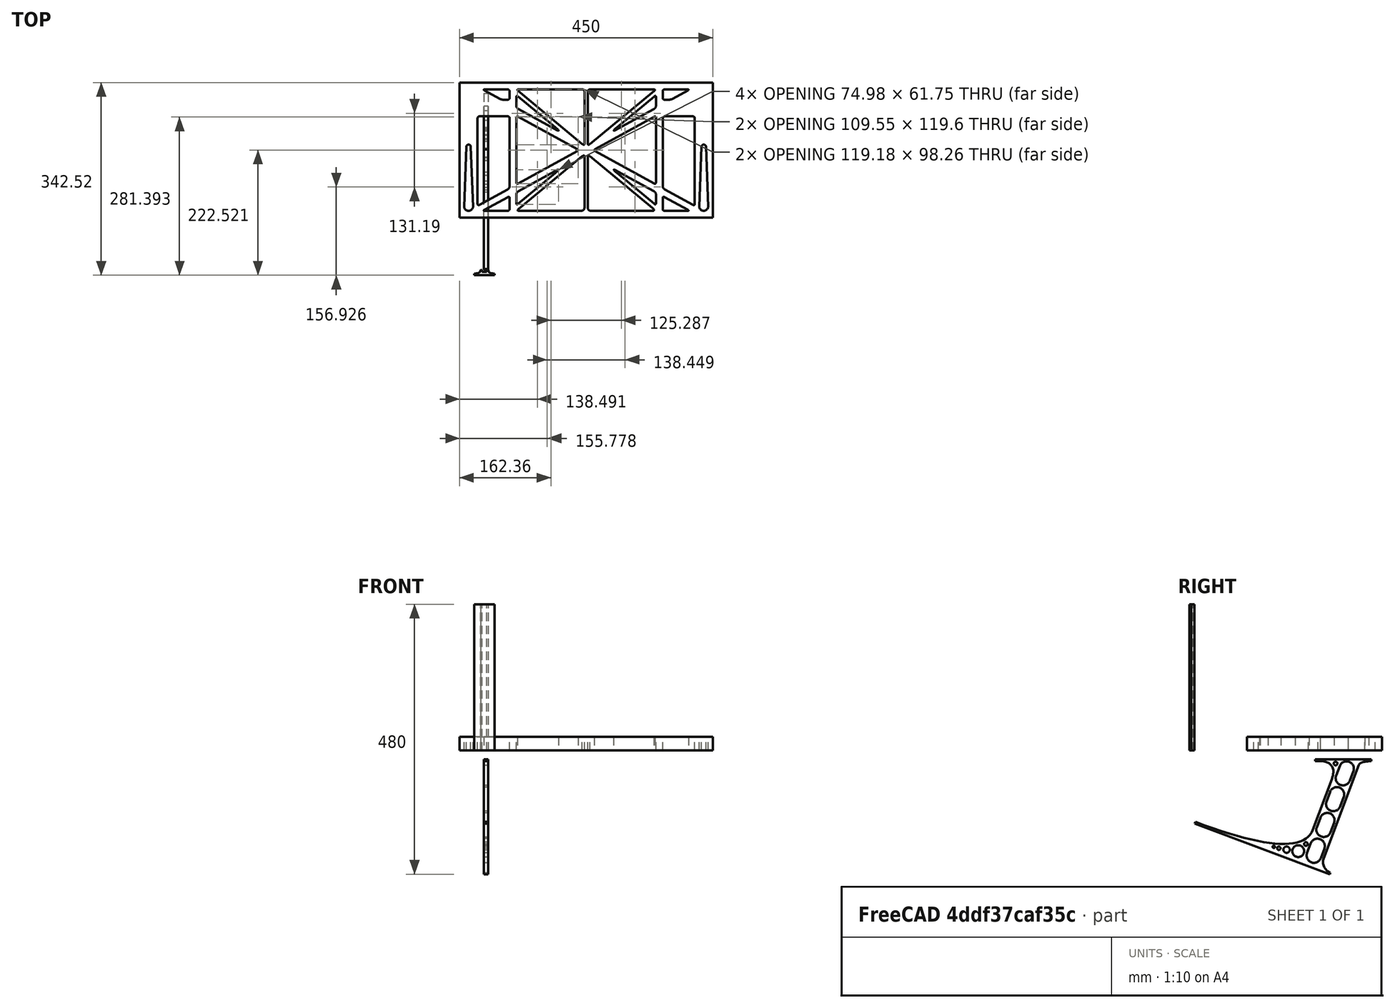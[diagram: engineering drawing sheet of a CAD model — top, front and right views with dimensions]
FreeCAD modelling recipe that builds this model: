
FCSTD DOCUMENT  (FreeCAD 0.19R0.19.2)
Label: laptopStand177FCStd
License: All rights reserved
LicenseURL: http://en.wikipedia.org/wiki/All_rights_reserved
objects: Sketcher::SketchObject×4, Part::Extrusion×3
note: 7 computed .brp shape members not serialized (recipe doc carries the construction recipe); baked Part::Feature solids carry a one-line shape summary decoded from their .brp

FEATURE [Sketcher::SketchObject] Sketch
  FullyConstrained = false
  sketch-geometry (349):
    g0: LineSegment StartX=-10.9272 StartY=-82.7794 StartZ=0 EndX=46.0728 EndY=-51.4823 EndZ=0
    g1: LineSegment StartX=-10.9272 StartY=76.4095 StartZ=0 EndX=-10.9272 EndY=-82.7794 EndZ=0
    g2: LineSegment StartX=46.0728 StartY=76.4095 StartZ=0 EndX=46.0728 EndY=-51.4823 EndZ=0
    g3: LineSegment StartX=-42.9272 StartY=136.221 StartZ=0 EndX=-42.9272 EndY=-103.779 EndZ=0
    g4: LineSegment StartX=407.073 StartY=136.221 StartZ=0 EndX=407.073 EndY=-103.779 EndZ=0
    g5: ArcOfCircle CenterX=-26.9272 CenterY=-83.7794 CenterZ=0 NormalX=0 NormalY=0 NormalZ=1 AngleXU=0 Radius=8 StartAngle=3.14159 EndAngle=6.28319
    g6: ArcOfCircle CenterX=391.073 CenterY=22.1087 CenterZ=0 NormalX=0 NormalY=0 NormalZ=1 AngleXU=0 Radius=8 StartAngle=-4.4e-15 EndAngle=3.14159
    g7: LineSegment StartX=399.073 StartY=22.1087 StartZ=0 EndX=399.073 EndY=-83.7794 EndZ=0
    g8: LineSegment StartX=383.073 StartY=22.1087 StartZ=0 EndX=383.073 EndY=-83.7794 EndZ=0
    g9: ArcOfCircle CenterX=391.073 CenterY=-83.7794 CenterZ=0 NormalX=0 NormalY=0 NormalZ=1 AngleXU=0 Radius=8 StartAngle=3.14159 EndAngle=6.28319
    g10: Circle CenterX=175.022 CenterY=27.0628 CenterZ=0 NormalX=0 NormalY=0 NormalZ=1 AngleXU=0 Radius=1
    g11: Circle CenterX=179.022 CenterY=24.8665 CenterZ=0 NormalX=0 NormalY=0 NormalZ=1 AngleXU=0 Radius=1
    g12: Circle CenterX=179.022 CenterY=27.0628 CenterZ=0 NormalX=0 NormalY=0 NormalZ=1 AngleXU=0 Radius=1
    g13: BSplineCurve PolesCount=3 KnotsCount=2 Degree=2 IsPeriodic=0
    g14: GeomPoint X=175.022 Y=27.0628 Z=0
    g15: GeomPoint X=179.022 Y=27.0628 Z=0
    g16: Circle CenterX=189.124 CenterY=27.0628 CenterZ=0 NormalX=0 NormalY=0 NormalZ=1 AngleXU=0 Radius=1
    g17: Circle CenterX=185.124 CenterY=24.8665 CenterZ=0 NormalX=0 NormalY=0 NormalZ=1 AngleXU=0 Radius=1
    g18: Circle CenterX=185.124 CenterY=27.0628 CenterZ=0 NormalX=0 NormalY=0 NormalZ=1 AngleXU=0 Radius=1
    g19: BSplineCurve PolesCount=3 KnotsCount=2 Degree=2 IsPeriodic=0
    g20: GeomPoint X=189.124 Y=27.0628 Z=0
    g21: GeomPoint X=185.124 Y=27.0628 Z=0
    g22: Circle CenterX=175.022 CenterY=5.37834 CenterZ=0 NormalX=0 NormalY=0 NormalZ=1 AngleXU=0 Radius=1
    g23: Circle CenterX=179.022 CenterY=7.57463 CenterZ=0 NormalX=0 NormalY=0 NormalZ=1 AngleXU=0 Radius=1
    g24: Circle CenterX=179.022 CenterY=5.34704 CenterZ=0 NormalX=0 NormalY=0 NormalZ=1 AngleXU=0 Radius=1
    g25: BSplineCurve PolesCount=3 KnotsCount=2 Degree=2 IsPeriodic=0
    g26: GeomPoint X=175.022 Y=5.37834 Z=0
    g27: GeomPoint X=179.022 Y=5.34704 Z=0
    g28: Circle CenterX=189.124 CenterY=5.37834 CenterZ=0 NormalX=0 NormalY=0 NormalZ=1 AngleXU=0 Radius=1
    g29: Circle CenterX=185.124 CenterY=7.57463 CenterZ=0 NormalX=0 NormalY=0 NormalZ=1 AngleXU=0 Radius=1
    g30: Circle CenterX=185.124 CenterY=5.34704 CenterZ=0 NormalX=0 NormalY=0 NormalZ=1 AngleXU=0 Radius=1
    g31: BSplineCurve PolesCount=3 KnotsCount=2 Degree=2 IsPeriodic=0
    g32: GeomPoint X=189.124 Y=5.37834 Z=0
    g33: GeomPoint X=185.124 Y=5.34704 Z=0
    g34: Circle CenterX=165.871 CenterY=18.1458 CenterZ=0 NormalX=0 NormalY=0 NormalZ=1 AngleXU=0 Radius=1
    g35: Circle CenterX=169.377 CenterY=16.2206 CenterZ=0 NormalX=0 NormalY=0 NormalZ=1 AngleXU=0 Radius=1
    g36: Circle CenterX=165.871 CenterY=14.2954 CenterZ=0 NormalX=0 NormalY=0 NormalZ=1 AngleXU=0 Radius=1
    g37: BSplineCurve PolesCount=3 KnotsCount=2 Degree=2 IsPeriodic=0
    g38: GeomPoint X=165.871 Y=18.1458 Z=0
    g39: GeomPoint X=165.871 Y=14.2954 Z=0
    g40: Circle CenterX=198.275 CenterY=18.1458 CenterZ=0 NormalX=0 NormalY=0 NormalZ=1 AngleXU=0 Radius=1
    g41: Circle CenterX=194.768 CenterY=16.2206 CenterZ=0 NormalX=0 NormalY=0 NormalZ=1 AngleXU=0 Radius=1
    g42: Circle CenterX=198.275 CenterY=14.2954 CenterZ=0 NormalX=0 NormalY=0 NormalZ=1 AngleXU=0 Radius=1
    g43: BSplineCurve PolesCount=3 KnotsCount=2 Degree=2 IsPeriodic=0
    g44: GeomPoint X=198.275 Y=18.1458 Z=0
    g45: GeomPoint X=198.275 Y=14.2954 Z=0
    g46: LineSegment StartX=407.073 StartY=-103.779 StartZ=0 EndX=-42.9272 EndY=-103.779 EndZ=0
    g47: LineSegment StartX=407.073 StartY=136.221 StartZ=0 EndX=-42.9272 EndY=136.221 EndZ=0
    g48: LineSegment StartX=46.0728 StartY=76.4095 StartZ=0 EndX=-10.9272 EndY=76.4095 EndZ=0
    g49: Circle CenterX=125.607 CenterY=54.1951 CenterZ=0 NormalX=0 NormalY=0 NormalZ=1 AngleXU=0 Radius=1
    g50: Circle CenterX=139.632 CenterY=46.4944 CenterZ=0 NormalX=0 NormalY=0 NormalZ=1 AngleXU=0 Radius=1
    g51: Circle CenterX=127.326 CenterY=56.7187 CenterZ=0 NormalX=0 NormalY=0 NormalZ=1 AngleXU=0 Radius=1
    g52: BSplineCurve PolesCount=3 KnotsCount=2 Degree=2 IsPeriodic=0
    g53: GeomPoint X=125.607 Y=54.1951 Z=0
    g54: GeomPoint X=127.326 Y=56.7187 Z=0
    g55: Circle CenterX=236.821 CenterY=56.7187 CenterZ=0 NormalX=0 NormalY=0 NormalZ=1 AngleXU=0 Radius=1
    g56: Circle CenterX=224.513 CenterY=46.4944 CenterZ=0 NormalX=0 NormalY=0 NormalZ=1 AngleXU=0 Radius=1
    g57: Circle CenterX=238.538 CenterY=54.1951 CenterZ=0 NormalX=0 NormalY=0 NormalZ=1 AngleXU=0 Radius=1
    g58: BSplineCurve PolesCount=3 KnotsCount=2 Degree=2 IsPeriodic=0
    g59: GeomPoint X=236.821 Y=56.7187 Z=0
    g60: GeomPoint X=238.538 Y=54.1951 Z=0
    g61: Circle CenterX=238.538 CenterY=-21.7539 CenterZ=0 NormalX=0 NormalY=0 NormalZ=1 AngleXU=0 Radius=1
    g62: Circle CenterX=224.513 CenterY=-14.0532 CenterZ=0 NormalX=0 NormalY=0 NormalZ=1 AngleXU=0 Radius=1
    g63: Circle CenterX=236.821 CenterY=-24.2775 CenterZ=0 NormalX=0 NormalY=0 NormalZ=1 AngleXU=0 Radius=1
    g64: BSplineCurve PolesCount=3 KnotsCount=2 Degree=2 IsPeriodic=0
    g65: GeomPoint X=238.538 Y=-21.7539 Z=0
    g66: GeomPoint X=236.821 Y=-24.2775 Z=0
    g67: Circle CenterX=125.607 CenterY=-21.7539 CenterZ=0 NormalX=0 NormalY=0 NormalZ=1 AngleXU=0 Radius=1
    g68: Circle CenterX=139.632 CenterY=-14.0532 CenterZ=0 NormalX=0 NormalY=0 NormalZ=1 AngleXU=0 Radius=1
    g69: Circle CenterX=127.325 CenterY=-24.2775 CenterZ=0 NormalX=0 NormalY=0 NormalZ=1 AngleXU=0 Radius=1
    g70: BSplineCurve PolesCount=3 KnotsCount=2 Degree=2 IsPeriodic=0
    g71: GeomPoint X=125.607 Y=-21.7539 Z=0
    g72: GeomPoint X=127.325 Y=-24.2775 Z=0
    g73: Circle CenterX=302.996 CenterY=111.695 CenterZ=0 NormalX=0 NormalY=0 NormalZ=1 AngleXU=0 Radius=1
    g74: Circle CenterX=306.073 CenterY=114.251 CenterZ=0 NormalX=0 NormalY=0 NormalZ=1 AngleXU=0 Radius=1
    g75: Circle CenterX=306.073 CenterY=110.251 CenterZ=0 NormalX=0 NormalY=0 NormalZ=1 AngleXU=0 Radius=1
    g76: BSplineCurve PolesCount=3 KnotsCount=2 Degree=2 IsPeriodic=0
    g77: GeomPoint X=302.996 Y=111.695 Z=0
    g78: GeomPoint X=306.073 Y=110.251 Z=0
    g79: Circle CenterX=306.073 CenterY=95.2763 CenterZ=0 NormalX=0 NormalY=0 NormalZ=1 AngleXU=0 Radius=1
    g80: Circle CenterX=306.073 CenterY=91.2763 CenterZ=0 NormalX=0 NormalY=0 NormalZ=1 AngleXU=0 Radius=1
    g81: Circle CenterX=302.567 CenterY=89.3511 CenterZ=0 NormalX=0 NormalY=0 NormalZ=1 AngleXU=0 Radius=1
    g82: BSplineCurve PolesCount=3 KnotsCount=2 Degree=2 IsPeriodic=0
    g83: GeomPoint X=306.073 Y=95.2763 Z=0
    g84: GeomPoint X=302.567 Y=89.3511 Z=0
    g85: LineSegment StartX=306.073 StartY=110.251 StartZ=0 EndX=306.073 EndY=95.2763 EndZ=0
    g86: LineSegment StartX=302.996 StartY=111.695 StartZ=0 EndX=236.821 EndY=56.7187 EndZ=0
    g87: LineSegment StartX=238.538 StartY=54.1951 StartZ=0 EndX=302.567 EndY=89.3511 EndZ=0
    g88: Circle CenterX=61.1496 CenterY=111.695 CenterZ=0 NormalX=0 NormalY=0 NormalZ=1 AngleXU=0 Radius=1
    g89: Circle CenterX=58.0728 CenterY=114.251 CenterZ=0 NormalX=0 NormalY=0 NormalZ=1 AngleXU=0 Radius=1
    g90: Circle CenterX=58.0728 CenterY=110.251 CenterZ=0 NormalX=0 NormalY=0 NormalZ=1 AngleXU=0 Radius=1
    g91: BSplineCurve PolesCount=3 KnotsCount=2 Degree=2 IsPeriodic=0
    g92: GeomPoint X=61.1496 Y=111.695 Z=0
    g93: GeomPoint X=58.0728 Y=110.251 Z=0
    g94: Circle CenterX=61.5791 CenterY=89.3511 CenterZ=0 NormalX=0 NormalY=0 NormalZ=1 AngleXU=0 Radius=1
    g95: Circle CenterX=58.0728 CenterY=91.2763 CenterZ=0 NormalX=0 NormalY=0 NormalZ=1 AngleXU=0 Radius=1
    g96: Circle CenterX=58.0728 CenterY=95.2763 CenterZ=0 NormalX=0 NormalY=0 NormalZ=1 AngleXU=0 Radius=1
    g97: BSplineCurve PolesCount=3 KnotsCount=2 Degree=2 IsPeriodic=0
    g98: GeomPoint X=61.5791 Y=89.3511 Z=0
    g99: GeomPoint X=58.0728 Y=95.2763 Z=0
    g100: LineSegment StartX=58.0728 StartY=110.251 StartZ=0 EndX=58.0728 EndY=95.2763 EndZ=0
    g101: LineSegment StartX=61.1496 StartY=111.695 StartZ=0 EndX=127.326 EndY=56.7187 EndZ=0
    g102: LineSegment StartX=125.607 StartY=54.1951 StartZ=0 EndX=61.5791 EndY=89.3511 EndZ=0
    g103: Circle CenterX=61.5791 CenterY=-56.9099 CenterZ=0 NormalX=0 NormalY=0 NormalZ=1 AngleXU=0 Radius=1
    g104: Circle CenterX=58.0728 CenterY=-58.8351 CenterZ=0 NormalX=0 NormalY=0 NormalZ=1 AngleXU=0 Radius=1
    g105: Circle CenterX=58.0728 CenterY=-62.8351 CenterZ=0 NormalX=0 NormalY=0 NormalZ=1 AngleXU=0 Radius=1
    g106: BSplineCurve PolesCount=3 KnotsCount=2 Degree=2 IsPeriodic=0
    g107: GeomPoint X=61.5791 Y=-56.9099 Z=0
    g108: GeomPoint X=58.0728 Y=-62.8351 Z=0
    g109: Circle CenterX=58.0728 CenterY=-77.8102 CenterZ=0 NormalX=0 NormalY=0 NormalZ=1 AngleXU=0 Radius=1
    g110: Circle CenterX=58.0728 CenterY=-81.8102 CenterZ=0 NormalX=0 NormalY=0 NormalZ=1 AngleXU=0 Radius=1
    g111: Circle CenterX=61.1496 CenterY=-79.2541 CenterZ=0 NormalX=0 NormalY=0 NormalZ=1 AngleXU=0 Radius=1
    g112: BSplineCurve PolesCount=3 KnotsCount=2 Degree=2 IsPeriodic=0
    g113: GeomPoint X=58.0728 Y=-77.8102 Z=0
    g114: GeomPoint X=61.1496 Y=-79.2541 Z=0
    g115: LineSegment StartX=58.0728 StartY=-62.8351 StartZ=0 EndX=58.0728 EndY=-77.8102 EndZ=0
    g116: LineSegment StartX=61.1496 StartY=-79.2541 StartZ=0 EndX=127.325 EndY=-24.2775 EndZ=0
    g117: LineSegment StartX=125.607 StartY=-21.7539 StartZ=0 EndX=61.5791 EndY=-56.9099 EndZ=0
    g118: Circle CenterX=302.567 CenterY=-56.9099 CenterZ=0 NormalX=0 NormalY=0 NormalZ=1 AngleXU=0 Radius=1
    g119: Circle CenterX=306.073 CenterY=-58.8351 CenterZ=0 NormalX=0 NormalY=0 NormalZ=1 AngleXU=0 Radius=1
    g120: Circle CenterX=306.073 CenterY=-62.8351 CenterZ=0 NormalX=0 NormalY=0 NormalZ=1 AngleXU=0 Radius=1
    g121: BSplineCurve PolesCount=3 KnotsCount=2 Degree=2 IsPeriodic=0
    g122: GeomPoint X=302.567 Y=-56.9099 Z=0
    g123: GeomPoint X=306.073 Y=-62.8351 Z=0
    g124: Circle CenterX=302.996 CenterY=-79.2541 CenterZ=0 NormalX=0 NormalY=0 NormalZ=1 AngleXU=0 Radius=1
    g125: Circle CenterX=306.073 CenterY=-81.8102 CenterZ=0 NormalX=0 NormalY=0 NormalZ=1 AngleXU=0 Radius=1
    g126: Circle CenterX=306.073 CenterY=-77.8102 CenterZ=0 NormalX=0 NormalY=0 NormalZ=1 AngleXU=0 Radius=1
    g127: BSplineCurve PolesCount=3 KnotsCount=2 Degree=2 IsPeriodic=0
    g128: GeomPoint X=302.996 Y=-79.2541 Z=0
    g129: GeomPoint X=306.073 Y=-77.8102 Z=0
    g130: LineSegment StartX=306.073 StartY=-62.8351 StartZ=0 EndX=306.073 EndY=-77.8102 EndZ=0
    g131: LineSegment StartX=302.996 StartY=-79.2541 StartZ=0 EndX=236.821 EndY=-24.2775 EndZ=0
    g132: LineSegment StartX=238.538 StartY=-21.7539 StartZ=0 EndX=302.567 EndY=-56.9099 EndZ=0
    g133: Circle CenterX=61.6457 CenterY=-88.8112 CenterZ=0 NormalX=0 NormalY=0 NormalZ=1 AngleXU=0 Radius=1
    g134: Circle CenterX=58.0728 CenterY=-91.7794 CenterZ=0 NormalX=0 NormalY=0 NormalZ=1 AngleXU=0 Radius=1
    g135: Circle CenterX=63.9135 CenterY=-91.7794 CenterZ=0 NormalX=0 NormalY=0 NormalZ=1 AngleXU=0 Radius=1
    g136: BSplineCurve PolesCount=3 KnotsCount=2 Degree=2 IsPeriodic=0
    g137: GeomPoint X=61.6457 Y=-88.8112 Z=0
    g138: GeomPoint X=63.9135 Y=-91.7794 Z=0
    g139: Circle CenterX=179.022 CenterY=-85.8163 CenterZ=0 NormalX=0 NormalY=0 NormalZ=1 AngleXU=0 Radius=1
    g140: Circle CenterX=179.022 CenterY=-91.7794 CenterZ=0 NormalX=0 NormalY=0 NormalZ=1 AngleXU=0 Radius=1
    g141: Circle CenterX=171.895 CenterY=-91.7794 CenterZ=0 NormalX=0 NormalY=0 NormalZ=1 AngleXU=0 Radius=1
    g142: BSplineCurve PolesCount=3 KnotsCount=2 Degree=2 IsPeriodic=0
    g143: GeomPoint X=179.022 Y=-85.8163 Z=0
    g144: GeomPoint X=171.895 Y=-91.7794 Z=0
    g145: Circle CenterX=185.124 CenterY=-86.2028 CenterZ=0 NormalX=0 NormalY=0 NormalZ=1 AngleXU=0 Radius=1
    g146: Circle CenterX=185.124 CenterY=-91.7794 CenterZ=0 NormalX=0 NormalY=0 NormalZ=1 AngleXU=0 Radius=1
    g147: Circle CenterX=191.747 CenterY=-91.7794 CenterZ=0 NormalX=0 NormalY=0 NormalZ=1 AngleXU=0 Radius=1
    g148: BSplineCurve PolesCount=3 KnotsCount=2 Degree=2 IsPeriodic=0
    g149: GeomPoint X=185.124 Y=-86.2028 Z=0
    g150: GeomPoint X=191.747 Y=-91.7794 Z=0
    g151: Circle CenterX=299.888 CenterY=-86.6413 CenterZ=0 NormalX=0 NormalY=0 NormalZ=1 AngleXU=0 Radius=1
    g152: Circle CenterX=306.073 CenterY=-91.7794 CenterZ=0 NormalX=0 NormalY=0 NormalZ=1 AngleXU=0 Radius=1
    g153: Circle CenterX=298.776 CenterY=-91.7794 CenterZ=0 NormalX=0 NormalY=0 NormalZ=1 AngleXU=0 Radius=1
    g154: BSplineCurve PolesCount=3 KnotsCount=2 Degree=2 IsPeriodic=0
    g155: GeomPoint X=299.888 Y=-86.6413 Z=0
    g156: GeomPoint X=298.776 Y=-91.7794 Z=0
    g157: LineSegment StartX=189.124 StartY=5.37834 StartZ=0 EndX=299.888 EndY=-86.6413 EndZ=0
    g158: LineSegment StartX=298.776 StartY=-91.7794 StartZ=0 EndX=191.747 EndY=-91.7794 EndZ=0
    g159: LineSegment StartX=185.124 StartY=-86.2028 StartZ=0 EndX=185.124 EndY=5.34704 EndZ=0
    g160: LineSegment StartX=179.022 StartY=5.34704 StartZ=0 EndX=179.022 EndY=-85.8163 EndZ=0
    g161: LineSegment StartX=171.895 StartY=-91.7794 StartZ=0 EndX=63.9135 EndY=-91.7794 EndZ=0
    g162: LineSegment StartX=61.6457 StartY=-88.8112 StartZ=0 EndX=175.022 EndY=5.37834 EndZ=0
    g163: Circle CenterX=302.073 CenterY=124.221 CenterZ=0 NormalX=0 NormalY=0 NormalZ=1 AngleXU=0 Radius=1
    g164: Circle CenterX=306.073 CenterY=124.221 CenterZ=0 NormalX=0 NormalY=0 NormalZ=1 AngleXU=0 Radius=1
    g165: Circle CenterX=302.996 CenterY=121.665 CenterZ=0 NormalX=0 NormalY=0 NormalZ=1 AngleXU=0 Radius=1
    g166: BSplineCurve PolesCount=3 KnotsCount=2 Degree=2 IsPeriodic=0
    g167: GeomPoint X=302.073 Y=124.221 Z=0
    g168: GeomPoint X=302.996 Y=121.665 Z=0
    g169: Circle CenterX=189.124 CenterY=124.221 CenterZ=0 NormalX=0 NormalY=0 NormalZ=1 AngleXU=0 Radius=1
    g170: Circle CenterX=185.124 CenterY=124.221 CenterZ=0 NormalX=0 NormalY=0 NormalZ=1 AngleXU=0 Radius=1
    g171: Circle CenterX=185.124 CenterY=120.221 CenterZ=0 NormalX=0 NormalY=0 NormalZ=1 AngleXU=0 Radius=1
    g172: BSplineCurve PolesCount=3 KnotsCount=2 Degree=2 IsPeriodic=0
    g173: GeomPoint X=189.124 Y=124.221 Z=0
    g174: GeomPoint X=185.124 Y=120.221 Z=0
    g175: Circle CenterX=175.022 CenterY=124.221 CenterZ=0 NormalX=0 NormalY=0 NormalZ=1 AngleXU=0 Radius=1
    g176: Circle CenterX=179.022 CenterY=124.221 CenterZ=0 NormalX=0 NormalY=0 NormalZ=1 AngleXU=0 Radius=1
    g177: Circle CenterX=179.022 CenterY=120.221 CenterZ=0 NormalX=0 NormalY=0 NormalZ=1 AngleXU=0 Radius=1
    g178: BSplineCurve PolesCount=3 KnotsCount=2 Degree=2 IsPeriodic=0
    g179: GeomPoint X=175.022 Y=124.221 Z=0
    g180: GeomPoint X=179.022 Y=120.221 Z=0
    g181: Circle CenterX=62.0728 CenterY=124.221 CenterZ=0 NormalX=0 NormalY=0 NormalZ=1 AngleXU=0 Radius=1
    g182: Circle CenterX=58.0728 CenterY=124.221 CenterZ=0 NormalX=0 NormalY=0 NormalZ=1 AngleXU=0 Radius=1
    g183: Circle CenterX=61.1496 CenterY=121.665 CenterZ=0 NormalX=0 NormalY=0 NormalZ=1 AngleXU=0 Radius=1
    g184: BSplineCurve PolesCount=3 KnotsCount=2 Degree=2 IsPeriodic=0
    g185: GeomPoint X=62.0728 Y=124.221 Z=0
    g186: GeomPoint X=61.1496 Y=121.665 Z=0
    g187: LineSegment StartX=62.0728 StartY=124.221 StartZ=0 EndX=175.022 EndY=124.221 EndZ=0
    g188: LineSegment StartX=179.022 StartY=120.221 StartZ=0 EndX=179.022 EndY=27.0628 EndZ=0
    g189: LineSegment StartX=185.124 StartY=27.0628 StartZ=0 EndX=185.124 EndY=120.221 EndZ=0
    g190: LineSegment StartX=189.124 StartY=124.221 StartZ=0 EndX=302.073 EndY=124.221 EndZ=0
    g191: LineSegment StartX=302.996 StartY=121.665 StartZ=0 EndX=189.124 EndY=27.0628 EndZ=0
    g192: LineSegment StartX=175.022 StartY=27.0628 StartZ=0 EndX=61.1496 EndY=121.665 EndZ=0
    g193: Circle CenterX=61.5791 CenterY=75.4095 CenterZ=0 NormalX=0 NormalY=0 NormalZ=1 AngleXU=0 Radius=1
    g194: Circle CenterX=58.0728 CenterY=77.3346 CenterZ=0 NormalX=0 NormalY=0 NormalZ=1 AngleXU=0 Radius=1
    g195: Circle CenterX=58.0728 CenterY=73.3346 CenterZ=0 NormalX=0 NormalY=0 NormalZ=1 AngleXU=0 Radius=1
    g196: BSplineCurve PolesCount=3 KnotsCount=2 Degree=2 IsPeriodic=0
    g197: GeomPoint X=61.5791 Y=75.4095 Z=0
    g198: GeomPoint X=58.0728 Y=73.3346 Z=0
    g199: Circle CenterX=58.0728 CenterY=-40.8935 CenterZ=0 NormalX=0 NormalY=0 NormalZ=1 AngleXU=0 Radius=1
    g200: Circle CenterX=58.0728 CenterY=-44.8935 CenterZ=0 NormalX=0 NormalY=0 NormalZ=1 AngleXU=0 Radius=1
    g201: Circle CenterX=61.5791 CenterY=-42.9683 CenterZ=0 NormalX=0 NormalY=0 NormalZ=1 AngleXU=0 Radius=1
    g202: BSplineCurve PolesCount=3 KnotsCount=2 Degree=2 IsPeriodic=0
    g203: GeomPoint X=58.0728 Y=-40.8935 Z=0
    g204: GeomPoint X=61.5791 Y=-42.9683 Z=0
    g205: LineSegment StartX=61.5791 StartY=-42.9683 StartZ=0 EndX=165.871 EndY=14.2954 EndZ=0
    g206: LineSegment StartX=165.871 StartY=18.1458 StartZ=0 EndX=61.5791 EndY=75.4095 EndZ=0
    g207: LineSegment StartX=58.0728 StartY=73.3346 StartZ=0 EndX=58.0728 EndY=-40.8935 EndZ=0
    g208: Circle CenterX=302.567 CenterY=-42.9683 CenterZ=0 NormalX=0 NormalY=0 NormalZ=1 AngleXU=0 Radius=1
    g209: Circle CenterX=306.073 CenterY=-44.8935 CenterZ=0 NormalX=0 NormalY=0 NormalZ=1 AngleXU=0 Radius=1
    g210: Circle CenterX=306.073 CenterY=-40.8935 CenterZ=0 NormalX=0 NormalY=0 NormalZ=1 AngleXU=0 Radius=1
    g211: BSplineCurve PolesCount=3 KnotsCount=2 Degree=2 IsPeriodic=0
    g212: GeomPoint X=302.567 Y=-42.9683 Z=0
    g213: GeomPoint X=306.073 Y=-40.8935 Z=0
    g214: Circle CenterX=306.073 CenterY=73.3346 CenterZ=0 NormalX=0 NormalY=0 NormalZ=1 AngleXU=0 Radius=1
    g215: Circle CenterX=306.073 CenterY=77.3346 CenterZ=0 NormalX=0 NormalY=0 NormalZ=1 AngleXU=0 Radius=1
    g216: Circle CenterX=302.567 CenterY=75.4095 CenterZ=0 NormalX=0 NormalY=0 NormalZ=1 AngleXU=0 Radius=1
    g217: BSplineCurve PolesCount=3 KnotsCount=2 Degree=2 IsPeriodic=0
    g218: GeomPoint X=306.073 Y=73.3346 Z=0
    g219: GeomPoint X=302.567 Y=75.4095 Z=0
    g220: LineSegment StartX=302.567 StartY=-42.9683 StartZ=0 EndX=198.275 EndY=14.2954 EndZ=0
    g221: LineSegment StartX=198.275 StartY=18.1458 StartZ=0 EndX=302.567 EndY=75.4095 EndZ=0
    g222: LineSegment StartX=306.073 StartY=73.3346 StartZ=0 EndX=306.073 EndY=-40.8935 EndZ=0
    g223: LineSegment StartX=322.073 StartY=105.865 StartZ=0 EndX=328.643 EndY=105.865 EndZ=0
    g224: LineSegment StartX=318.073 StartY=120.221 StartZ=0 EndX=318.073 EndY=109.865 EndZ=0
    g225: LineSegment StartX=336.157 StartY=107.779 StartZ=0 EndX=362.567 EndY=122.294 EndZ=0
    g226: Circle CenterX=362.073 CenterY=124.221 CenterZ=0 NormalX=0 NormalY=0 NormalZ=1 AngleXU=0 Radius=1
    g227: Circle CenterX=366.073 CenterY=124.221 CenterZ=0 NormalX=0 NormalY=0 NormalZ=1 AngleXU=0 Radius=1
    g228: Circle CenterX=362.567 CenterY=122.294 CenterZ=0 NormalX=0 NormalY=0 NormalZ=1 AngleXU=0 Radius=1
    g229: BSplineCurve PolesCount=3 KnotsCount=2 Degree=2 IsPeriodic=0
    g230: GeomPoint X=362.073 Y=124.221 Z=0
    g231: GeomPoint X=362.567 Y=122.294 Z=0
    g232: Circle CenterX=322.073 CenterY=124.221 CenterZ=0 NormalX=0 NormalY=0 NormalZ=1 AngleXU=0 Radius=1
    g233: Circle CenterX=318.073 CenterY=124.221 CenterZ=0 NormalX=0 NormalY=0 NormalZ=1 AngleXU=0 Radius=1
    g234: Circle CenterX=318.073 CenterY=120.221 CenterZ=0 NormalX=0 NormalY=0 NormalZ=1 AngleXU=0 Radius=1
    g235: BSplineCurve PolesCount=3 KnotsCount=2 Degree=2 IsPeriodic=0
    g236: GeomPoint X=322.073 Y=124.221 Z=0
    g237: GeomPoint X=318.073 Y=120.221 Z=0
    g238: Circle CenterX=322.073 CenterY=105.865 CenterZ=0 NormalX=0 NormalY=0 NormalZ=1 AngleXU=0 Radius=1
    g239: Circle CenterX=318.073 CenterY=105.865 CenterZ=0 NormalX=0 NormalY=0 NormalZ=1 AngleXU=0 Radius=1
    g240: Circle CenterX=318.073 CenterY=109.865 CenterZ=0 NormalX=0 NormalY=0 NormalZ=1 AngleXU=0 Radius=1
    g241: BSplineCurve PolesCount=3 KnotsCount=2 Degree=2 IsPeriodic=0
    g242: GeomPoint X=322.073 Y=105.865 Z=0
    g243: GeomPoint X=318.073 Y=109.865 Z=0
    g244: Circle CenterX=336.157 CenterY=107.779 CenterZ=0 NormalX=0 NormalY=0 NormalZ=1 AngleXU=0 Radius=1
    g245: Circle CenterX=332.651 CenterY=105.853 CenterZ=0 NormalX=0 NormalY=0 NormalZ=1 AngleXU=0 Radius=1
    g246: Circle CenterX=328.643 CenterY=105.865 CenterZ=0 NormalX=0 NormalY=0 NormalZ=1 AngleXU=0 Radius=1
    g247: BSplineCurve PolesCount=3 KnotsCount=2 Degree=2 IsPeriodic=0
    g248: GeomPoint X=336.157 Y=107.779 Z=0
    g249: GeomPoint X=328.643 Y=105.865 Z=0
    g250: LineSegment StartX=322.073 StartY=124.221 StartZ=0 EndX=362.073 EndY=124.221 EndZ=0
    g251: Circle CenterX=371.567 CenterY=-80.8644 CenterZ=0 NormalX=0 NormalY=0 NormalZ=1 AngleXU=0 Radius=1
    g252: Circle CenterX=375.073 CenterY=-82.7896 CenterZ=0 NormalX=0 NormalY=0 NormalZ=1 AngleXU=0 Radius=1
    g253: Circle CenterX=375.073 CenterY=-78.7896 CenterZ=0 NormalX=0 NormalY=0 NormalZ=1 AngleXU=0 Radius=1
    g254: BSplineCurve PolesCount=3 KnotsCount=2 Degree=2 IsPeriodic=0
    g255: GeomPoint X=371.567 Y=-80.8644 Z=0
    g256: GeomPoint X=375.073 Y=-78.7896 Z=0
    g257: Circle CenterX=321.579 CenterY=-53.4075 CenterZ=0 NormalX=0 NormalY=0 NormalZ=1 AngleXU=0 Radius=1
    g258: Circle CenterX=318.073 CenterY=-51.4823 CenterZ=0 NormalX=0 NormalY=0 NormalZ=1 AngleXU=0 Radius=1
    g259: Circle CenterX=318.073 CenterY=-47.4805 CenterZ=0 NormalX=0 NormalY=0 NormalZ=1 AngleXU=0 Radius=1
    g260: BSplineCurve PolesCount=3 KnotsCount=2 Degree=2 IsPeriodic=0
    g261: GeomPoint X=321.579 Y=-53.4075 Z=0
    g262: GeomPoint X=318.073 Y=-47.4805 Z=0
    g263: LineSegment StartX=371.567 StartY=-80.8644 StartZ=0 EndX=321.579 EndY=-53.4075 EndZ=0
    g264: Circle CenterX=321.579 CenterY=-67.3492 CenterZ=0 NormalX=0 NormalY=0 NormalZ=1 AngleXU=0 Radius=1
    g265: Circle CenterX=318.073 CenterY=-65.424 CenterZ=0 NormalX=0 NormalY=0 NormalZ=1 AngleXU=0 Radius=1
    g266: Circle CenterX=318.073 CenterY=-69.424 CenterZ=0 NormalX=0 NormalY=0 NormalZ=1 AngleXU=0 Radius=1
    g267: BSplineCurve PolesCount=3 KnotsCount=2 Degree=2 IsPeriodic=0
    g268: GeomPoint X=321.579 Y=-67.3492 Z=0
    g269: GeomPoint X=318.073 Y=-69.424 Z=0
    g270: Circle CenterX=362.567 CenterY=-89.8542 CenterZ=0 NormalX=0 NormalY=0 NormalZ=1 AngleXU=0 Radius=1
    g271: Circle CenterX=366.073 CenterY=-91.7794 CenterZ=0 NormalX=0 NormalY=0 NormalZ=1 AngleXU=0 Radius=1
    g272: Circle CenterX=362.073 CenterY=-91.7794 CenterZ=0 NormalX=0 NormalY=0 NormalZ=1 AngleXU=0 Radius=1
    g273: BSplineCurve PolesCount=3 KnotsCount=2 Degree=2 IsPeriodic=0
    g274: GeomPoint X=362.567 Y=-89.8542 Z=0
    g275: GeomPoint X=362.073 Y=-91.7794 Z=0
    g276: Circle CenterX=322.073 CenterY=-91.7794 CenterZ=0 NormalX=0 NormalY=0 NormalZ=1 AngleXU=0 Radius=1
    g277: Circle CenterX=318.073 CenterY=-91.7794 CenterZ=0 NormalX=0 NormalY=0 NormalZ=1 AngleXU=0 Radius=1
    g278: Circle CenterX=318.073 CenterY=-87.7794 CenterZ=0 NormalX=0 NormalY=0 NormalZ=1 AngleXU=0 Radius=1
    g279: BSplineCurve PolesCount=3 KnotsCount=2 Degree=2 IsPeriodic=0
    g280: GeomPoint X=322.073 Y=-91.7794 Z=0
    g281: GeomPoint X=318.073 Y=-87.7794 Z=0
    g282: LineSegment StartX=362.567 StartY=-89.8542 StartZ=0 EndX=321.579 EndY=-67.3492 EndZ=0
    g283: LineSegment StartX=318.073 StartY=-69.424 StartZ=0 EndX=318.073 EndY=-87.7794 EndZ=0
    g284: LineSegment StartX=322.073 StartY=-91.7794 StartZ=0 EndX=362.073 EndY=-91.7794 EndZ=0
    g285: Circle CenterX=2.07281 CenterY=124.221 CenterZ=0 NormalX=0 NormalY=0 NormalZ=1 AngleXU=0 Radius=1
    g286: Circle CenterX=1.57905 CenterY=122.295 CenterZ=0 NormalX=0 NormalY=0 NormalZ=1 AngleXU=0 Radius=1
    g287: BSplineCurve PolesCount=3 KnotsCount=2 Degree=2 IsPeriodic=0
    g288: GeomPoint X=2.07281 Y=124.221 Z=0
    g289: GeomPoint X=1.57905 Y=122.295 Z=0
    g290: Circle CenterX=42.0728 CenterY=124.221 CenterZ=0 NormalX=0 NormalY=0 NormalZ=1 AngleXU=0 Radius=1
    g291: Circle CenterX=46.0728 CenterY=124.221 CenterZ=0 NormalX=0 NormalY=0 NormalZ=1 AngleXU=0 Radius=1
    g292: Circle CenterX=46.0728 CenterY=120.221 CenterZ=0 NormalX=0 NormalY=0 NormalZ=1 AngleXU=0 Radius=1
    g293: BSplineCurve PolesCount=3 KnotsCount=2 Degree=2 IsPeriodic=0
    g294: GeomPoint X=42.0728 Y=124.221 Z=0
    g295: GeomPoint X=46.0728 Y=120.221 Z=0
    g296: Circle CenterX=46.0728 CenterY=109.865 CenterZ=0 NormalX=0 NormalY=0 NormalZ=1 AngleXU=0 Radius=1
    g297: Circle CenterX=46.0728 CenterY=105.865 CenterZ=0 NormalX=0 NormalY=0 NormalZ=1 AngleXU=0 Radius=1
    g298: Circle CenterX=42.0728 CenterY=105.865 CenterZ=0 NormalX=0 NormalY=0 NormalZ=1 AngleXU=0 Radius=1
    g299: BSplineCurve PolesCount=3 KnotsCount=2 Degree=2 IsPeriodic=0
    g300: GeomPoint X=46.0728 Y=109.865 Z=0
    g301: GeomPoint X=42.0728 Y=105.865 Z=0
    g302: Circle CenterX=35.5028 CenterY=105.865 CenterZ=0 NormalX=0 NormalY=0 NormalZ=1 AngleXU=0 Radius=1
    g303: Circle CenterX=31.5028 CenterY=105.865 CenterZ=0 NormalX=0 NormalY=0 NormalZ=1 AngleXU=0 Radius=1
    g304: Circle CenterX=27.9965 CenterY=107.79 CenterZ=0 NormalX=0 NormalY=0 NormalZ=1 AngleXU=0 Radius=1
    g305: BSplineCurve PolesCount=3 KnotsCount=2 Degree=2 IsPeriodic=0
    g306: GeomPoint X=35.5028 Y=105.865 Z=0
    g307: GeomPoint X=27.9965 Y=107.79 Z=0
    g308: LineSegment StartX=2.07281 StartY=124.221 StartZ=0 EndX=42.0728 EndY=124.221 EndZ=0
    g309: LineSegment StartX=46.0728 StartY=120.221 StartZ=0 EndX=46.0728 EndY=109.865 EndZ=0
    g310: LineSegment StartX=42.0728 StartY=105.865 StartZ=0 EndX=35.5028 EndY=105.865 EndZ=0
    g311: LineSegment StartX=27.9965 StartY=107.79 StartZ=0 EndX=1.57905 EndY=122.295 EndZ=0
    g312: Circle CenterX=42.5666 CenterY=-67.3492 CenterZ=0 NormalX=0 NormalY=0 NormalZ=1 AngleXU=0 Radius=1
    g313: Circle CenterX=46.0728 CenterY=-65.424 CenterZ=0 NormalX=0 NormalY=0 NormalZ=1 AngleXU=0 Radius=1
    g314: Circle CenterX=46.0728 CenterY=-69.424 CenterZ=0 NormalX=0 NormalY=0 NormalZ=1 AngleXU=0 Radius=1
    g315: BSplineCurve PolesCount=3 KnotsCount=2 Degree=2 IsPeriodic=0
    g316: GeomPoint X=42.5666 Y=-67.3492 Z=0
    g317: GeomPoint X=46.0728 Y=-69.424 Z=0
    g318: Circle CenterX=46.0728 CenterY=-87.7794 CenterZ=0 NormalX=0 NormalY=0 NormalZ=1 AngleXU=0 Radius=1
    g319: Circle CenterX=46.0728 CenterY=-91.7794 CenterZ=0 NormalX=0 NormalY=0 NormalZ=1 AngleXU=0 Radius=1
    g320: Circle CenterX=42.0728 CenterY=-91.7794 CenterZ=0 NormalX=0 NormalY=0 NormalZ=1 AngleXU=0 Radius=1
    g321: BSplineCurve PolesCount=3 KnotsCount=2 Degree=2 IsPeriodic=0
    g322: GeomPoint X=46.0728 Y=-87.7794 Z=0
    g323: GeomPoint X=42.0728 Y=-91.7794 Z=0
    g324: Circle CenterX=2.07281 CenterY=-91.7794 CenterZ=0 NormalX=0 NormalY=0 NormalZ=1 AngleXU=0 Radius=1
    g325: Circle CenterX=-1.92719 CenterY=-91.7794 CenterZ=0 NormalX=0 NormalY=0 NormalZ=1 AngleXU=0 Radius=1
    g326: Circle CenterX=1.57905 CenterY=-89.8542 CenterZ=0 NormalX=0 NormalY=0 NormalZ=1 AngleXU=0 Radius=1
    g327: BSplineCurve PolesCount=3 KnotsCount=2 Degree=2 IsPeriodic=0
    g328: GeomPoint X=2.07281 Y=-91.7794 Z=0
    g329: GeomPoint X=1.57905 Y=-89.8542 Z=0
    g330: LineSegment StartX=2.07281 StartY=-91.7794 StartZ=0 EndX=42.0728 EndY=-91.7794 EndZ=0
    g331: LineSegment StartX=46.0728 StartY=-87.7794 StartZ=0 EndX=46.0728 EndY=-69.424 EndZ=0
    g332: LineSegment StartX=42.5666 StartY=-67.3492 StartZ=0 EndX=1.57905 EndY=-89.8542 EndZ=0
    g333: Circle CenterX=322.073 CenterY=76.4095 CenterZ=0 NormalX=0 NormalY=0 NormalZ=1 AngleXU=0 Radius=4
    g334: BSplineCurve PolesCount=3 KnotsCount=2 Degree=2 IsPeriodic=0
    g335: GeomPoint X=318.073 Y=72.4095 Z=0
    g336: GeomPoint X=322.073 Y=76.4095 Z=0
    g337: Circle CenterX=375.073 CenterY=72.4095 CenterZ=0 NormalX=0 NormalY=0 NormalZ=1 AngleXU=0 Radius=1
    g338: Circle CenterX=375.073 CenterY=76.4095 CenterZ=0 NormalX=0 NormalY=0 NormalZ=1 AngleXU=0 Radius=1
    g339: Circle CenterX=371.073 CenterY=76.4095 CenterZ=0 NormalX=0 NormalY=0 NormalZ=1 AngleXU=0 Radius=1
    g340: BSplineCurve PolesCount=3 KnotsCount=2 Degree=2 IsPeriodic=0
    g341: GeomPoint X=375.073 Y=72.4095 Z=0
    g342: GeomPoint X=371.073 Y=76.4095 Z=0
    g343: LineSegment StartX=322.073 StartY=76.4095 StartZ=0 EndX=371.073 EndY=76.4095 EndZ=0
    g344: LineSegment StartX=318.073 StartY=72.4095 StartZ=0 EndX=318.073 EndY=-47.4805 EndZ=0
    g345: LineSegment StartX=375.073 StartY=72.4095 StartZ=0 EndX=375.073 EndY=-78.7896 EndZ=0
    g346: ArcOfCircle CenterX=-26.9272 CenterY=22.1087 CenterZ=0 NormalX=0 NormalY=0 NormalZ=1 AngleXU=0 Radius=4 StartAngle=5e-16 EndAngle=3.14159
    g347: LineSegment StartX=-30.9272 StartY=22.1087 StartZ=0 EndX=-34.9272 EndY=-83.7794 EndZ=0
    g348: LineSegment StartX=-18.9272 StartY=-83.7794 StartZ=0 EndX=-22.9272 EndY=22.1087 EndZ=0
  constraints (572):
    c: Coincident(g0,g2)
    c: Block(g0)
    c: Block(g1)
    c: Vertical(g3)
    c: Vertical(g4)
    c: Block(g4)
    c: Block(g3)
    c: Tangent(g6,g7) = 1.5708
    c: Tangent(g7,g9) = 1.5708
    c: Equal(g6,g9)
    c: Coincident(g8,g6)
    c: Coincident(g8,g9)
    c: Block(g7)
    c: Block(g8)
    c: Weight(g10) = 1
    c: Equal(g10,g11)
    c: Equal(g10,g12)
    c: InternalAlignment(g10,g13)
    c: InternalAlignment(g11,g13)
    c: InternalAlignment(g12,g13)
    c: InternalAlignment(g14,g13)
    c: InternalAlignment(g15,g13)
    c: Weight(g16) = 1
    c: Equal(g16,g17)
    c: Equal(g16,g18)
    c: InternalAlignment(g16,g19)
    c: InternalAlignment(g17,g19)
    c: InternalAlignment(g18,g19)
    c: InternalAlignment(g20,g19)
    c: InternalAlignment(g21,g19)
    c: Block(g19)
    c: Block(g13)
    c: Weight(g22) = 1
    c: Equal(g22,g23)
    c: Equal(g22,g24)
    c: InternalAlignment(g22,g25)
    c: InternalAlignment(g23,g25)
    c: InternalAlignment(g24,g25)
    c: InternalAlignment(g26,g25)
    c: InternalAlignment(g27,g25)
    c: Weight(g28) = 1
    c: Equal(g28,g29)
    c: Equal(g28,g30)
    c: InternalAlignment(g28,g31)
    c: InternalAlignment(g29,g31)
    c: InternalAlignment(g30,g31)
    c: InternalAlignment(g32,g31)
    c: InternalAlignment(g33,g31)
    c: Block(g31)
    c: Block(g25)
    c: Weight(g34) = 1
    c: Equal(g34,g35)
    c: Equal(g34,g36)
    c: InternalAlignment(g34,g37)
    c: InternalAlignment(g35,g37)
    c: InternalAlignment(g36,g37)
    c: InternalAlignment(g38,g37)
    c: InternalAlignment(g39,g37)
    c: Weight(g40) = 1
    c: Equal(g40,g41)
    c: Equal(g40,g42)
    c: InternalAlignment(g40,g43)
    c: InternalAlignment(g41,g43)
    c: InternalAlignment(g42,g43)
    c: InternalAlignment(g44,g43)
    c: InternalAlignment(g45,g43)
    c: Block(g37)
    c: Block(g43)
    c: Coincident(g46,g4)
    c: Coincident(g46,g3)
    c: Horizontal(g46)
    c: Distance(g46) = 450
    c: Coincident(g47,g4)
    c: Coincident(g47,g3)
    c: Horizontal(g47)
    c: Horizontal(g48)
    c: Coincident(g2,g48)
    c: Block(g48)
    c: Coincident(g1,g48)
    c: Weight(g49) = 1
    c: Equal(g49,g50)
    c: Equal(g49,g51)
    c: InternalAlignment(g49,g52)
    c: InternalAlignment(g50,g52)
    c: InternalAlignment(g51,g52)
    c: InternalAlignment(g53,g52)
    c: InternalAlignment(g54,g52)
    c: Block(g52)
    c: Weight(g55) = 1
    c: Equal(g55,g56)
    c: Equal(g55,g57)
    c: InternalAlignment(g55,g58)
    c: InternalAlignment(g56,g58)
    c: InternalAlignment(g57,g58)
    c: InternalAlignment(g59,g58)
    c: InternalAlignment(g60,g58)
    c: Block(g58)
    c: Weight(g61) = 1
    c: Equal(g61,g62)
    c: Equal(g61,g63)
    c: InternalAlignment(g61,g64)
    c: InternalAlignment(g62,g64)
    c: InternalAlignment(g63,g64)
    c: InternalAlignment(g65,g64)
    c: InternalAlignment(g66,g64)
    c: Block(g64)
    c: Weight(g67) = 1
    c: Equal(g67,g68)
    c: Equal(g67,g69)
    c: InternalAlignment(g67,g70)
    c: InternalAlignment(g68,g70)
    c: InternalAlignment(g69,g70)
    c: InternalAlignment(g71,g70)
    c: InternalAlignment(g72,g70)
    c: Block(g70)
    c: Weight(g73) = 1
    c: Equal(g73,g74)
    c: Equal(g73,g75)
    c: InternalAlignment(g73,g76)
    c: InternalAlignment(g74,g76)
    c: InternalAlignment(g75,g76)
    c: InternalAlignment(g77,g76)
    c: InternalAlignment(g78,g76)
    c: Weight(g79) = 1
    c: Equal(g79,g80)
    c: Equal(g79,g81)
    c: InternalAlignment(g79,g82)
    c: InternalAlignment(g80,g82)
    c: InternalAlignment(g81,g82)
    c: InternalAlignment(g83,g82)
    c: InternalAlignment(g84,g82)
    c: Block(g76)
    c: Block(g82)
    c: Coincident(g85,g76)
    c: Coincident(g85,g82)
    c: Vertical(g85)
    c: Coincident(g86,g76)
    c: Coincident(g86,g58)
    c: Coincident(g87,g58)
    c: Coincident(g87,g82)
    c: Weight(g88) = 1
    c: Equal(g88,g89)
    c: Equal(g88,g90)
    c: InternalAlignment(g88,g91)
    c: InternalAlignment(g89,g91)
    c: InternalAlignment(g90,g91)
    c: InternalAlignment(g92,g91)
    c: InternalAlignment(g93,g91)
    c: Weight(g94) = 1
    c: Equal(g94,g95)
    c: Equal(g94,g96)
    c: InternalAlignment(g94,g97)
    c: InternalAlignment(g95,g97)
    c: InternalAlignment(g96,g97)
    c: InternalAlignment(g98,g97)
    c: InternalAlignment(g99,g97)
    c: Block(g91)
    c: Block(g97)
    c: Coincident(g100,g91)
    c: Coincident(g100,g97)
    c: Vertical(g100)
    c: Coincident(g101,g91)
    c: Coincident(g101,g52)
    c: Coincident(g102,g52)
    c: Coincident(g102,g97)
    c: Weight(g103) = 1
    c: Equal(g103,g104)
    c: Equal(g103,g105)
    c: InternalAlignment(g103,g106)
    c: InternalAlignment(g104,g106)
    c: InternalAlignment(g105,g106)
    c: InternalAlignment(g107,g106)
    c: InternalAlignment(g108,g106)
    c: Weight(g109) = 1
    c: Equal(g109,g110)
    c: Equal(g109,g111)
    c: InternalAlignment(g109,g112)
    c: InternalAlignment(g110,g112)
    c: InternalAlignment(g111,g112)
    c: InternalAlignment(g113,g112)
    c: InternalAlignment(g114,g112)
    c: Block(g106)
    c: Block(g112)
    c: Coincident(g115,g106)
    c: Coincident(g115,g112)
    c: Vertical(g115)
    c: Coincident(g116,g112)
    c: Coincident(g116,g70)
    c: Coincident(g117,g70)
    c: Coincident(g117,g106)
    c: Weight(g118) = 1
    c: Equal(g118,g119)
    c: Equal(g118,g120)
    c: InternalAlignment(g118,g121)
    c: InternalAlignment(g119,g121)
    c: InternalAlignment(g120,g121)
    c: InternalAlignment(g122,g121)
    c: InternalAlignment(g123,g121)
    c: Weight(g124) = 1
    c: Equal(g124,g125)
    c: Equal(g124,g126)
    c: InternalAlignment(g124,g127)
    c: InternalAlignment(g125,g127)
    c: InternalAlignment(g126,g127)
    c: InternalAlignment(g128,g127)
    c: InternalAlignment(g129,g127)
    c: Block(g121)
    c: Block(g127)
    c: Coincident(g130,g121)
    c: Coincident(g130,g127)
    c: Vertical(g130)
    c: Coincident(g131,g127)
    c: Coincident(g131,g64)
    c: Coincident(g132,g64)
    c: Coincident(g132,g121)
    c: Weight(g133) = 1
    c: Equal(g133,g134)
    c: Equal(g133,g135)
    c: InternalAlignment(g133,g136)
    c: InternalAlignment(g134,g136)
    c: InternalAlignment(g135,g136)
    c: InternalAlignment(g137,g136)
    c: InternalAlignment(g138,g136)
    c: Weight(g139) = 1
    c: Equal(g139,g140)
    c: Equal(g139,g141)
    c: InternalAlignment(g139,g142)
    c: InternalAlignment(g140,g142)
    c: InternalAlignment(g141,g142)
    c: InternalAlignment(g143,g142)
    c: InternalAlignment(g144,g142)
    c: Weight(g145) = 1
    c: Equal(g145,g146)
    c: Equal(g145,g147)
    c: InternalAlignment(g145,g148)
    c: InternalAlignment(g146,g148)
    c: InternalAlignment(g147,g148)
    c: InternalAlignment(g149,g148)
    c: InternalAlignment(g150,g148)
    c: Weight(g151) = 1
    c: Equal(g151,g152)
    c: Equal(g151,g153)
    c: InternalAlignment(g151,g154)
    c: InternalAlignment(g152,g154)
    c: InternalAlignment(g153,g154)
    c: InternalAlignment(g155,g154)
    c: InternalAlignment(g156,g154)
    c: Block(g154)
    c: Block(g148)
    c: Block(g142)
    c: Block(g136)
    c: Coincident(g157,g31)
    c: Coincident(g157,g154)
    c: Coincident(g158,g154)
    c: Coincident(g158,g148)
    c: Horizontal(g158)
    c: Coincident(g159,g148)
    c: Coincident(g159,g31)
    c: Vertical(g159)
    c: Coincident(g160,g25)
    c: Coincident(g160,g142)
    c: Vertical(g160)
    c: Coincident(g161,g142)
    c: Coincident(g161,g136)
    c: Horizontal(g161)
    c: Coincident(g162,g136)
    c: Coincident(g162,g25)
    c: Weight(g163) = 1
    c: Equal(g163,g164)
    c: Equal(g163,g165)
    c: InternalAlignment(g163,g166)
    c: InternalAlignment(g164,g166)
    c: InternalAlignment(g165,g166)
    c: InternalAlignment(g167,g166)
    c: InternalAlignment(g168,g166)
    c: Weight(g169) = 1
    c: Equal(g169,g170)
    c: Equal(g169,g171)
    c: InternalAlignment(g169,g172)
    c: InternalAlignment(g170,g172)
    c: InternalAlignment(g171,g172)
    c: InternalAlignment(g173,g172)
    c: InternalAlignment(g174,g172)
    c: Weight(g175) = 1
    c: Equal(g175,g176)
    c: Equal(g175,g177)
    c: InternalAlignment(g175,g178)
    c: InternalAlignment(g176,g178)
    c: InternalAlignment(g177,g178)
    c: InternalAlignment(g179,g178)
    c: InternalAlignment(g180,g178)
    c: Weight(g181) = 1
    c: Equal(g181,g182)
    c: Equal(g181,g183)
    c: InternalAlignment(g181,g184)
    c: InternalAlignment(g182,g184)
    c: InternalAlignment(g183,g184)
    c: InternalAlignment(g185,g184)
    c: InternalAlignment(g186,g184)
    c: Block(g184)
    c: Block(g178)
    c: Block(g172)
    c: Block(g166)
    c: Coincident(g187,g184)
    c: Coincident(g187,g178)
    c: Horizontal(g187)
    c: Coincident(g188,g178)
    c: Coincident(g188,g13)
    c: Vertical(g188)
    c: Coincident(g189,g19)
    c: Coincident(g189,g172)
    c: Vertical(g189)
    c: Coincident(g190,g172)
    c: Coincident(g190,g166)
    c: Horizontal(g190)
    c: Coincident(g191,g166)
    c: Coincident(g191,g19)
    c: Coincident(g192,g13)
    c: Weight(g193) = 1
    c: Equal(g193,g194)
    c: Equal(g193,g195)
    c: InternalAlignment(g193,g196)
    c: InternalAlignment(g194,g196)
    c: InternalAlignment(g195,g196)
    c: InternalAlignment(g197,g196)
    c: InternalAlignment(g198,g196)
    c: Weight(g199) = 1
    c: Equal(g199,g200)
    c: Equal(g199,g201)
    c: InternalAlignment(g199,g202)
    c: InternalAlignment(g200,g202)
    c: InternalAlignment(g201,g202)
    c: InternalAlignment(g203,g202)
    c: InternalAlignment(g204,g202)
    c: Block(g202)
    c: Block(g196)
    c: Coincident(g205,g202)
    c: Coincident(g205,g37)
    c: Coincident(g206,g37)
    c: Coincident(g206,g196)
    c: Coincident(g207,g196)
    c: Coincident(g207,g202)
    c: Vertical(g207)
    c: Weight(g208) = 1
    c: Equal(g208,g209)
    c: Equal(g208,g210)
    c: InternalAlignment(g208,g211)
    c: InternalAlignment(g209,g211)
    c: InternalAlignment(g210,g211)
    c: InternalAlignment(g212,g211)
    c: InternalAlignment(g213,g211)
    c: Weight(g214) = 1
    c: Equal(g214,g215)
    c: Equal(g214,g216)
    c: InternalAlignment(g214,g217)
    c: InternalAlignment(g215,g217)
    c: InternalAlignment(g216,g217)
    c: InternalAlignment(g218,g217)
    c: InternalAlignment(g219,g217)
    c: Block(g217)
    c: Block(g211)
    c: Coincident(g220,g211)
    c: Coincident(g220,g43)
    c: Coincident(g221,g43)
    c: Coincident(g221,g217)
    c: Coincident(g222,g217)
    c: Coincident(g222,g211)
    c: Vertical(g222)
    c: Horizontal(g223)
    c: Block(g223)
    c: Vertical(g224)
    c: Block(g224)
    c: Block(g225)
    c: Weight(g226) = 1
    c: Equal(g226,g227)
    c: Equal(g226,g228)
    c: InternalAlignment(g226,g229)
    c: InternalAlignment(g227,g229)
    c: InternalAlignment(g228,g229)
    c: InternalAlignment(g230,g229)
    c: InternalAlignment(g231,g229)
    c: Weight(g232) = 1
    c: Equal(g232,g233)
    c: Equal(g232,g234)
    c: InternalAlignment(g232,g235)
    c: InternalAlignment(g233,g235)
    c: InternalAlignment(g234,g235)
    c: InternalAlignment(g236,g235)
    c: InternalAlignment(g237,g235)
    c: Weight(g238) = 1
    c: Equal(g238,g239)
    c: Equal(g238,g240)
    c: InternalAlignment(g238,g241)
    c: InternalAlignment(g239,g241)
    c: InternalAlignment(g240,g241)
    c: InternalAlignment(g242,g241)
    c: InternalAlignment(g243,g241)
    c: Weight(g244) = 1
    c: Equal(g244,g245)
    c: Equal(g244,g246)
    c: InternalAlignment(g244,g247)
    c: InternalAlignment(g245,g247)
    c: InternalAlignment(g246,g247)
    c: InternalAlignment(g248,g247)
    c: InternalAlignment(g249,g247)
    c: Block(g229)
    c: Block(g235)
    c: Block(g241)
    c: Block(g247)
    c: Coincident(g250,g235)
    c: Coincident(g250,g229)
    c: Horizontal(g250)
    c: Block(g192)
    c: Weight(g251) = 1
    c: Equal(g251,g252)
    c: Equal(g251,g253)
    c: InternalAlignment(g251,g254)
    c: InternalAlignment(g252,g254)
    c: InternalAlignment(g253,g254)
    c: InternalAlignment(g255,g254)
    c: InternalAlignment(g256,g254)
    c: Weight(g257) = 1
    c: Equal(g257,g258)
    c: Equal(g257,g259)
    c: InternalAlignment(g257,g260)
    c: InternalAlignment(g258,g260)
    c: InternalAlignment(g259,g260)
    c: InternalAlignment(g261,g260)
    c: InternalAlignment(g262,g260)
    c: Block(g254)
    c: Block(g260)
    c: Coincident(g263,g254)
    c: Coincident(g263,g260)
    c: Weight(g264) = 1
    c: Equal(g264,g265)
    c: Equal(g264,g266)
    c: InternalAlignment(g264,g267)
    c: InternalAlignment(g265,g267)
    c: InternalAlignment(g266,g267)
    c: InternalAlignment(g268,g267)
    c: InternalAlignment(g269,g267)
    c: Weight(g270) = 1
    c: Equal(g270,g271)
    c: Equal(g270,g272)
    c: InternalAlignment(g270,g273)
    c: InternalAlignment(g271,g273)
    c: InternalAlignment(g272,g273)
    c: InternalAlignment(g274,g273)
    c: InternalAlignment(g275,g273)
    c: Weight(g276) = 1
    c: Equal(g276,g277)
    c: Equal(g276,g278)
    c: InternalAlignment(g276,g279)
    c: InternalAlignment(g277,g279)
    c: InternalAlignment(g278,g279)
    c: InternalAlignment(g280,g279)
    c: InternalAlignment(g281,g279)
    c: Block(g279)
    c: Block(g273)
    c: Block(g267)
    c: Coincident(g282,g273)
    c: Coincident(g282,g267)
    c: Coincident(g283,g267)
    c: Coincident(g283,g279)
    c: Vertical(g283)
    c: Coincident(g284,g279)
    c: Coincident(g284,g273)
    c: Horizontal(g284)
    c: Weight(g285) = 1
    c: Equal(g285,g286)
    c: InternalAlignment(g285,g287)
    c: InternalAlignment(g286,g287)
    c: InternalAlignment(g288,g287)
    c: InternalAlignment(g289,g287)
    c: Weight(g290) = 1
    c: InternalAlignment(g291,g293)
    c: InternalAlignment(g292,g293)
    c: InternalAlignment(g294,g293)
    c: InternalAlignment(g295,g293)
    c: Weight(g296) = 1
    c: Equal(g296,g297)
    c: Equal(g296,g298)
    c: InternalAlignment(g296,g299)
    c: InternalAlignment(g297,g299)
    c: InternalAlignment(g298,g299)
    c: InternalAlignment(g300,g299)
    c: InternalAlignment(g301,g299)
    c: Equal(g302,g303)
    c: Equal(g302,g304)
    c: InternalAlignment(g302,g305)
    c: InternalAlignment(g303,g305)
    c: InternalAlignment(g304,g305)
    c: InternalAlignment(g306,g305)
    c: InternalAlignment(g307,g305)
    c: Block(g293)
    c: Block(g299)
    c: Block(g305)
    c: Block(g287)
    c: Coincident(g308,g287)
    c: Coincident(g308,g293)
    c: Horizontal(g308)
    c: Coincident(g309,g293)
    c: Coincident(g309,g299)
    c: Vertical(g309)
    c: Coincident(g310,g299)
    c: Coincident(g310,g305)
    c: Horizontal(g310)
    c: Coincident(g311,g305)
    c: Coincident(g311,g287)
    c: Weight(g312) = 1
    c: Equal(g312,g313)
    c: Equal(g312,g314)
    c: InternalAlignment(g312,g315)
    c: InternalAlignment(g313,g315)
    c: InternalAlignment(g314,g315)
    c: InternalAlignment(g316,g315)
    c: InternalAlignment(g317,g315)
    c: Weight(g318) = 1
    c: Equal(g318,g319)
    c: Equal(g318,g320)
    c: InternalAlignment(g318,g321)
    c: InternalAlignment(g319,g321)
    c: InternalAlignment(g320,g321)
    c: InternalAlignment(g322,g321)
    c: InternalAlignment(g323,g321)
    c: Weight(g324) = 1
    c: Equal(g324,g325)
    c: Equal(g324,g326)
    c: InternalAlignment(g324,g327)
    c: InternalAlignment(g325,g327)
    c: InternalAlignment(g326,g327)
    c: InternalAlignment(g328,g327)
    c: InternalAlignment(g329,g327)
    c: Block(g327)
    c: Block(g321)
    c: Block(g315)
    c: Coincident(g330,g327)
    c: Coincident(g330,g321)
    c: Horizontal(g330)
    c: Coincident(g331,g321)
    c: Coincident(g331,g315)
    c: Vertical(g331)
    c: Coincident(g332,g315)
    c: Coincident(g332,g327)
    c: InternalAlignment(g333,g334)
    c: InternalAlignment(g335,g334)
    c: InternalAlignment(g336,g334)
    c: Block(g334)
    c: Equal(g337,g338)
    c: Equal(g337,g339)
    c: InternalAlignment(g337,g340)
    c: InternalAlignment(g338,g340)
    c: InternalAlignment(g339,g340)
    c: InternalAlignment(g341,g340)
    c: InternalAlignment(g342,g340)
    c: Block(g340)
    c: Coincident(g343,g334)
    c: Horizontal(g343)
    c: Block(g343)
    c: Coincident(g344,g334)
    c: Coincident(g344,g260)
    c: Vertical(g344)
    c: Coincident(g345,g340)
    c: Coincident(g345,g254)
    c: Vertical(g345)
    c: Coincident(g347,g5)
    c: Coincident(g348,g5)
    c: Block(g346)
    c: Block(g5)
    c: Block(g348)
    c: Block(g347)
    c: Distance(g344) = 119.89
FEATURE [Sketcher::SketchObject] Sketch001
  FullyConstrained = true
  MapMode = 4
  Placement = pos=(0,0,0) rot=(0.57735,0.57735,0.57735;2.0944rad)
  Support = -> [Sketch]
  sketch-geometry (46):
    g0: BSplineCurve PolesCount=3 KnotsCount=2 Degree=2 IsPeriodic=0
    g1: ArcOfCircle CenterX=73.1223 CenterY=-32.291 CenterZ=0 NormalX=0 NormalY=0 NormalZ=1 AngleXU=0 Radius=13 StartAngle=5.92268 EndAngle=9.06428
    g2: ArcOfCircle CenterX=66.7816 CenterY=-49.1439 CenterZ=0 NormalX=0 NormalY=0 NormalZ=1 AngleXU=0 Radius=13 StartAngle=2.78068 EndAngle=5.92131
    g3: ArcOfCircle CenterX=55.9263 CenterY=-78.1807 CenterZ=0 NormalX=0 NormalY=0 NormalZ=1 AngleXU=0 Radius=13 StartAngle=5.92268 EndAngle=9.06428
    g4: ArcOfCircle CenterX=49.5884 CenterY=-95.0342 CenterZ=0 NormalX=0 NormalY=0 NormalZ=1 AngleXU=0 Radius=13 StartAngle=2.78068 EndAngle=5.92131
    g5: ArcOfCircle CenterX=38.7206 CenterY=-124.067 CenterZ=0 NormalX=0 NormalY=0 NormalZ=1 AngleXU=0 Radius=13 StartAngle=5.92268 EndAngle=9.06428
    g6: ArcOfCircle CenterX=32.3875 CenterY=-140.92 CenterZ=0 NormalX=0 NormalY=0 NormalZ=1 AngleXU=0 Radius=13 StartAngle=2.78068 EndAngle=5.92131
    g7: ArcOfCircle CenterX=21.4715 CenterY=-169.934 CenterZ=0 NormalX=0 NormalY=0 NormalZ=1 AngleXU=0 Radius=13 StartAngle=5.92268 EndAngle=9.06428
    g8: ArcOfCircle CenterX=15.1336 CenterY=-186.787 CenterZ=0 NormalX=0 NormalY=0 NormalZ=1 AngleXU=0 Radius=13 StartAngle=2.78068 EndAngle=5.92131
    g9-g12: Circle x4 (B-spline internal-alignment scaffolding for g13; pole/knot coordinates omitted)
    g13: BSplineCurve PolesCount=4 KnotsCount=2 Degree=3 IsPeriodic=0
    g14: GeomPoint X=28.8094 Y=-19.0875 Z=0
    g15: GeomPoint X=47.0443 Y=-50.4712 Z=0
    g16: Circle CenterX=53.5586 CenterY=-23.2695 CenterZ=0 NormalX=0 NormalY=0 NormalZ=1 AngleXU=0 Radius=3.24518
    g17: Circle CenterX=-195.441 CenterY=-127.082 CenterZ=0 NormalX=0 NormalY=0 NormalZ=1 AngleXU=0 Radius=1
    g18: Circle CenterX=-8.24091 CenterY=-197.481 CenterZ=0 NormalX=0 NormalY=0 NormalZ=1 AngleXU=0 Radius=1
    g19: Circle CenterX=12.8789 CenterY=-141.321 CenterZ=0 NormalX=0 NormalY=0 NormalZ=1 AngleXU=0 Radius=1
    g20: BSplineCurve PolesCount=3 KnotsCount=2 Degree=2 IsPeriodic=0
    g21: GeomPoint X=-195.441 Y=-127.082 Z=0
    g22: GeomPoint X=12.8789 Y=-141.321 Z=0
    g23: Circle CenterX=-12.8016 CenterY=-179.036 CenterZ=0 NormalX=0 NormalY=0 NormalZ=1 AngleXU=0 Radius=10.5072
    g24: Circle CenterX=0.933922 CenterY=-166.43 CenterZ=0 NormalX=0 NormalY=0 NormalZ=1 AngleXU=0 Radius=3.26661
    g25: Circle CenterX=-33.5518 CenterY=-176.44 CenterZ=0 NormalX=0 NormalY=0 NormalZ=1 AngleXU=0 Radius=5.64388
    g26: Circle CenterX=-47.2366 CenterY=-173.859 CenterZ=0 NormalX=0 NormalY=0 NormalZ=1 AngleXU=0 Radius=3.01653
    g27: Circle CenterX=-56.2595 CenterY=-171.456 CenterZ=0 NormalX=0 NormalY=0 NormalZ=1 AngleXU=0 Radius=2.12826
    g28: ArcOfCircle CenterX=51.2151 CenterY=-198.473 CenterZ=0 NormalX=0 NormalY=0 NormalZ=1 AngleXU=0 Radius=20 StartAngle=2.78189 EndAngle=4.35269
    g29: LineSegment StartX=32.4951 StartY=-191.433 StartZ=0 EndX=94.6578 EndY=-26.1352 EndZ=0
    g30: LineSegment StartX=43.1192 StartY=-220.001 StartZ=0 EndX=-196.497 EndY=-129.89 EndZ=0
    g31: LineSegment StartX=43.1192 StartY=-220.001 StartZ=0 EndX=44.1752 EndY=-217.193 EndZ=0
    g32: LineSegment StartX=117.223 StartY=-19.0875 StartZ=0 EndX=117.223 EndY=-16.0875 EndZ=0
    g33: LineSegment StartX=117.223 StartY=-16.0875 StartZ=0 EndX=17.2232 EndY=-16.0875 EndZ=0
    g34: LineSegment StartX=17.2232 StartY=-16.0875 StartZ=0 EndX=17.2232 EndY=-19.0875 EndZ=0
    g35: LineSegment StartX=28.8094 StartY=-19.0875 StartZ=0 EndX=17.2232 EndY=-19.0875 EndZ=0
    g36: LineSegment StartX=47.0443 StartY=-50.4712 StartZ=0 EndX=12.8789 EndY=-141.321 EndZ=0
    g37: LineSegment StartX=-195.441 StartY=-127.082 StartZ=0 EndX=-196.497 EndY=-129.89 EndZ=0
    g38: LineSegment StartX=85.2866 StartY=-36.8766 StartZ=0 EndX=78.9396 EndY=-53.7463 EndZ=0
    g39: LineSegment StartX=60.9579 StartY=-27.7053 StartZ=0 EndX=54.6191 EndY=-44.5532 EndZ=0
    g40: LineSegment StartX=68.0907 StartY=-82.7664 StartZ=0 EndX=61.7465 EndY=-99.6365 EndZ=0
    g41: LineSegment StartX=43.7619 StartY=-73.595 StartZ=0 EndX=37.426 EndY=-90.4435 EndZ=0
    g42: LineSegment StartX=50.885 StartY=-128.652 StartZ=0 EndX=44.5456 EndY=-145.522 EndZ=0
    g43: LineSegment StartX=26.5562 StartY=-119.481 StartZ=0 EndX=20.2251 EndY=-136.329 EndZ=0
    g44: LineSegment StartX=9.3071 StartY=-165.349 StartZ=0 EndX=2.97115 EndY=-182.197 EndZ=0
    g45: LineSegment StartX=33.6358 StartY=-174.52 StartZ=0 EndX=27.2917 EndY=-191.39 EndZ=0
  constraints (71):
    c: Block(g0)
    c: Block(g1)
    c: Block(g2)
    c: Block(g4)
    c: Block(g3)
    c: Block(g6)
    c: Block(g5)
    c: Block(g8)
    c: Block(g7)
    c: Weight(g9) = 1
    c: Equal(g9,g10)
    c: Equal(g9,g11)
    c: Equal(g9,g12)
    c: InternalAlignment(g9-g12 -> g13) x4
    c: InternalAlignment(g14,g13)
    c: InternalAlignment(g15,g13)
    c: Block(g16)
    c: Weight(g17) = 1
    c: Equal(g17,g18)
    c: Equal(g17,g19)
    c: InternalAlignment(g17,g20)
    c: InternalAlignment(g18,g20)
    c: InternalAlignment(g19,g20)
    c: InternalAlignment(g21,g20)
    c: InternalAlignment(g22,g20)
    c: Block(g20)
    c: Block(g23)
    c: Block(g24)
    c: Block(g25)
    c: Block(g26)
    c: Block(g27)
    c: Block(g28)
    c: Coincident(g29,g28)
    c: Coincident(g29,g0)
    c: Block(g13)
    c: Coincident(g31,g30)
    c: Coincident(g31,g28)
    c: Block(g31)
    c: Coincident(g32,g0)
    c: Vertical(g32)
    c: Coincident(g33,g32)
    c: Horizontal(g33)
    c: Coincident(g34,g33)
    c: Vertical(g34)
    c: Block(g33)
    c: Coincident(g35,g13)
    c: Coincident(g35,g34)
    c: Horizontal(g35)
    c: Coincident(g36,g13)
    c: Coincident(g36,g20)
    c: Coincident(g37,g20)
    c: Coincident(g37,g30)
    c: Block(g30)
    c: Coincident(g38,g1)
    c: Coincident(g38,g2)
    c: Coincident(g39,g1)
    c: Coincident(g39,g2)
    c: Coincident(g40,g3)
    c: Coincident(g40,g4)
    c: Coincident(g41,g3)
    c: Coincident(g41,g4)
    c: Coincident(g42,g5)
    c: Coincident(g42,g6)
    c: Coincident(g43,g5)
    c: Coincident(g43,g6)
    c: Coincident(g44,g7)
    c: Coincident(g44,g8)
    c: Coincident(g45,g7)
    c: Coincident(g45,g8)
    c: Distance(g30) = 256
    c: Distance(g33) = 100
FEATURE [Part::Extrusion] Extrude002
  Base = -> Sketch001
  Dir = (1,0,0)
  DirMode = 2
  FaceMakerClass = Part::FaceMakerBullseye
  LengthFwd = 8
  LengthRev = 0
  Solid = true
  Symmetric = false
FEATURE [Sketcher::SketchObject] Sketch002
  FullyConstrained = true
  sketch-geometry (20):
    g0: LineSegment StartX=-2.77179 StartY=-200.304 StartZ=0 EndX=5.22821 EndY=-200.304 EndZ=0
    g1: LineSegment StartX=5.22821 StartY=-200.304 StartZ=0 EndX=5.22821 EndY=-197.304 EndZ=0
    g2: LineSegment StartX=-2.77179 StartY=-200.304 StartZ=0 EndX=-2.77179 EndY=-197.304 EndZ=0
    g3: LineSegment StartX=5.22821 StartY=-197.304 StartZ=0 EndX=8.22821 EndY=-197.304 EndZ=0
    g4: LineSegment StartX=-2.77179 StartY=-197.304 StartZ=0 EndX=-5.77179 EndY=-197.304 EndZ=0
    g5: LineSegment StartX=19.2282 StartY=-203.304 StartZ=0 EndX=19.2282 EndY=-206.304 EndZ=0
    g6: LineSegment StartX=-16.7718 StartY=-203.304 StartZ=0 EndX=-16.7718 EndY=-206.304 EndZ=0
    g7: LineSegment StartX=-16.7718 StartY=-206.304 StartZ=0 EndX=19.2282 EndY=-206.304 EndZ=0
    g8: Circle CenterX=-16.7718 CenterY=-203.304 CenterZ=0 NormalX=0 NormalY=0 NormalZ=1 AngleXU=0 Radius=1
    g9: Circle CenterX=-5.77179 CenterY=-203.304 CenterZ=0 NormalX=0 NormalY=0 NormalZ=1 AngleXU=0 Radius=1
    g10: Circle CenterX=-5.77179 CenterY=-197.304 CenterZ=0 NormalX=0 NormalY=0 NormalZ=1 AngleXU=0 Radius=1
    g11: BSplineCurve PolesCount=3 KnotsCount=2 Degree=2 IsPeriodic=0
    g12: GeomPoint X=-16.7718 Y=-203.304 Z=0
    g13: GeomPoint X=-5.77179 Y=-197.304 Z=0
    g14: Circle CenterX=19.2282 CenterY=-203.304 CenterZ=0 NormalX=0 NormalY=0 NormalZ=1 AngleXU=0 Radius=1
    g15: Circle CenterX=8.22821 CenterY=-203.304 CenterZ=0 NormalX=0 NormalY=0 NormalZ=1 AngleXU=0 Radius=1
    g16: Circle CenterX=8.22821 CenterY=-197.304 CenterZ=0 NormalX=0 NormalY=0 NormalZ=1 AngleXU=0 Radius=1
    g17: BSplineCurve PolesCount=3 KnotsCount=2 Degree=2 IsPeriodic=0
    g18: GeomPoint X=19.2282 Y=-203.304 Z=0
    g19: GeomPoint X=8.22821 Y=-197.304 Z=0
  constraints (41):
    c: Horizontal(g0)
    c: Distance(g0) = 8
    c: Coincident(g1,g0)
    c: Vertical(g1)
    c: Distance(g1) = 3
    c: Coincident(g2,g0)
    c: Vertical(g2)
    c: Distance(g2) = 3
    c: Coincident(g3,g1)
    c: Horizontal(g3)
    c: Distance(g3) = 3
    c: Coincident(g4,g2)
    c: Horizontal(g4)
    c: Distance(g4) = 3
    c: Vertical(g5)
    c: Vertical(g6)
    c: Coincident(g7,g6)
    c: Coincident(g7,g5)
    c: Weight(g8) = 1
    c: Equal(g8,g9)
    c: Equal(g8,g10)
    c: Coincident(g11,g4)
    c: InternalAlignment(g8,g11)
    c: InternalAlignment(g9,g11)
    c: InternalAlignment(g10,g11)
    c: InternalAlignment(g12,g11)
    c: InternalAlignment(g13,g11)
    c: Coincident(g17,g5)
    c: Weight(g14) = 1
    c: Equal(g14,g15)
    c: Equal(g14,g16)
    c: Coincident(g17,g3)
    c: InternalAlignment(g14,g17)
    c: InternalAlignment(g15,g17)
    c: InternalAlignment(g16,g17)
    c: InternalAlignment(g18,g17)
    c: InternalAlignment(g19,g17)
    c: Block(g7)
    c: Block(g17)
    c: Block(g11)
    c: Block(g6)
FEATURE [Part::Extrusion] Extrude003
  Base = -> Sketch002
  Dir = (0,0,1)
  DirMode = 2
  FaceMakerClass = Part::FaceMakerBullseye
  LengthFwd = 260
  LengthRev = 0
  Solid = true
  Symmetric = false
FEATURE [Sketcher::SketchObject] Sketch003
  FullyConstrained = false
  sketch-geometry (427):
    g0: LineSegment StartX=-42.9272 StartY=136.221 StartZ=0 EndX=-42.9272 EndY=-103.779 EndZ=0
    g1: LineSegment StartX=407.073 StartY=136.221 StartZ=0 EndX=407.073 EndY=-103.779 EndZ=0
    g2: ArcOfCircle CenterX=-26.9272 CenterY=-83.7794 CenterZ=0 NormalX=0 NormalY=0 NormalZ=1 AngleXU=0 Radius=8 StartAngle=3.14159 EndAngle=6.28319
    g3: ArcOfCircle CenterX=391.073 CenterY=-83.7794 CenterZ=0 NormalX=0 NormalY=0 NormalZ=1 AngleXU=0 Radius=8 StartAngle=3.14159 EndAngle=6.28319
    g4: Circle CenterX=175.022 CenterY=27.0628 CenterZ=0 NormalX=0 NormalY=0 NormalZ=1 AngleXU=0 Radius=1
    g5: Circle CenterX=179.022 CenterY=24.8665 CenterZ=0 NormalX=0 NormalY=0 NormalZ=1 AngleXU=0 Radius=1
    g6: Circle CenterX=179.022 CenterY=27.0628 CenterZ=0 NormalX=0 NormalY=0 NormalZ=1 AngleXU=0 Radius=1
    g7: BSplineCurve PolesCount=3 KnotsCount=2 Degree=2 IsPeriodic=0
    g8: GeomPoint X=175.022 Y=27.0628 Z=0
    g9: GeomPoint X=179.022 Y=27.0628 Z=0
    g10: Circle CenterX=189.124 CenterY=27.0628 CenterZ=0 NormalX=0 NormalY=0 NormalZ=1 AngleXU=0 Radius=1
    g11: Circle CenterX=185.124 CenterY=24.8665 CenterZ=0 NormalX=0 NormalY=0 NormalZ=1 AngleXU=0 Radius=1
    g12: Circle CenterX=185.124 CenterY=27.0628 CenterZ=0 NormalX=0 NormalY=0 NormalZ=1 AngleXU=0 Radius=1
    g13: BSplineCurve PolesCount=3 KnotsCount=2 Degree=2 IsPeriodic=0
    g14: GeomPoint X=189.124 Y=27.0628 Z=0
    g15: GeomPoint X=185.124 Y=27.0628 Z=0
    g16: Circle CenterX=175.022 CenterY=5.37834 CenterZ=0 NormalX=0 NormalY=0 NormalZ=1 AngleXU=0 Radius=1
    g17: Circle CenterX=179.022 CenterY=7.57463 CenterZ=0 NormalX=0 NormalY=0 NormalZ=1 AngleXU=0 Radius=1
    g18: Circle CenterX=179.022 CenterY=5.34704 CenterZ=0 NormalX=0 NormalY=0 NormalZ=1 AngleXU=0 Radius=1
    g19: BSplineCurve PolesCount=3 KnotsCount=2 Degree=2 IsPeriodic=0
    g20: GeomPoint X=175.022 Y=5.37834 Z=0
    g21: GeomPoint X=179.022 Y=5.34704 Z=0
    g22: Circle CenterX=189.124 CenterY=5.37834 CenterZ=0 NormalX=0 NormalY=0 NormalZ=1 AngleXU=0 Radius=1
    g23: Circle CenterX=185.124 CenterY=7.57463 CenterZ=0 NormalX=0 NormalY=0 NormalZ=1 AngleXU=0 Radius=1
    g24: Circle CenterX=185.124 CenterY=5.34704 CenterZ=0 NormalX=0 NormalY=0 NormalZ=1 AngleXU=0 Radius=1
    g25: BSplineCurve PolesCount=3 KnotsCount=2 Degree=2 IsPeriodic=0
    g26: GeomPoint X=189.124 Y=5.37834 Z=0
    g27: GeomPoint X=185.124 Y=5.34704 Z=0
    g28: Circle CenterX=165.871 CenterY=18.1458 CenterZ=0 NormalX=0 NormalY=0 NormalZ=1 AngleXU=0 Radius=1
    g29: Circle CenterX=169.377 CenterY=16.2206 CenterZ=0 NormalX=0 NormalY=0 NormalZ=1 AngleXU=0 Radius=1
    g30: Circle CenterX=165.871 CenterY=14.2954 CenterZ=0 NormalX=0 NormalY=0 NormalZ=1 AngleXU=0 Radius=1
    g31: BSplineCurve PolesCount=3 KnotsCount=2 Degree=2 IsPeriodic=0
    g32: GeomPoint X=165.871 Y=18.1458 Z=0
    g33: GeomPoint X=165.871 Y=14.2954 Z=0
    g34: Circle CenterX=198.275 CenterY=18.1458 CenterZ=0 NormalX=0 NormalY=0 NormalZ=1 AngleXU=0 Radius=1
    g35: Circle CenterX=194.768 CenterY=16.2206 CenterZ=0 NormalX=0 NormalY=0 NormalZ=1 AngleXU=0 Radius=1
    g36: Circle CenterX=198.275 CenterY=14.2954 CenterZ=0 NormalX=0 NormalY=0 NormalZ=1 AngleXU=0 Radius=1
    g37: BSplineCurve PolesCount=3 KnotsCount=2 Degree=2 IsPeriodic=0
    g38: GeomPoint X=198.275 Y=18.1458 Z=0
    g39: GeomPoint X=198.275 Y=14.2954 Z=0
    g40: LineSegment StartX=407.073 StartY=-103.779 StartZ=0 EndX=-42.9272 EndY=-103.779 EndZ=0
    g41: Circle CenterX=125.607 CenterY=54.1951 CenterZ=0 NormalX=0 NormalY=0 NormalZ=1 AngleXU=0 Radius=1
    g42: Circle CenterX=139.632 CenterY=46.4944 CenterZ=0 NormalX=0 NormalY=0 NormalZ=1 AngleXU=0 Radius=1
    g43: Circle CenterX=127.326 CenterY=56.7187 CenterZ=0 NormalX=0 NormalY=0 NormalZ=1 AngleXU=0 Radius=1
    g44: BSplineCurve PolesCount=3 KnotsCount=2 Degree=2 IsPeriodic=0
    g45: GeomPoint X=125.607 Y=54.1951 Z=0
    g46: GeomPoint X=127.326 Y=56.7187 Z=0
    g47: Circle CenterX=236.821 CenterY=56.7187 CenterZ=0 NormalX=0 NormalY=0 NormalZ=1 AngleXU=0 Radius=1
    g48: Circle CenterX=224.513 CenterY=46.4944 CenterZ=0 NormalX=0 NormalY=0 NormalZ=1 AngleXU=0 Radius=1
    g49: Circle CenterX=238.538 CenterY=54.1951 CenterZ=0 NormalX=0 NormalY=0 NormalZ=1 AngleXU=0 Radius=1
    g50: BSplineCurve PolesCount=3 KnotsCount=2 Degree=2 IsPeriodic=0
    g51: GeomPoint X=236.821 Y=56.7187 Z=0
    g52: GeomPoint X=238.538 Y=54.1951 Z=0
    g53: Circle CenterX=238.538 CenterY=-21.7539 CenterZ=0 NormalX=0 NormalY=0 NormalZ=1 AngleXU=0 Radius=1
    g54: Circle CenterX=224.513 CenterY=-14.0532 CenterZ=0 NormalX=0 NormalY=0 NormalZ=1 AngleXU=0 Radius=1
    g55: Circle CenterX=236.821 CenterY=-24.2775 CenterZ=0 NormalX=0 NormalY=0 NormalZ=1 AngleXU=0 Radius=1
    g56: BSplineCurve PolesCount=3 KnotsCount=2 Degree=2 IsPeriodic=0
    g57: GeomPoint X=238.538 Y=-21.7539 Z=0
    g58: GeomPoint X=236.821 Y=-24.2775 Z=0
    g59: Circle CenterX=125.607 CenterY=-21.7539 CenterZ=0 NormalX=0 NormalY=0 NormalZ=1 AngleXU=0 Radius=1
    g60: Circle CenterX=139.632 CenterY=-14.0532 CenterZ=0 NormalX=0 NormalY=0 NormalZ=1 AngleXU=0 Radius=1
    g61: Circle CenterX=127.325 CenterY=-24.2775 CenterZ=0 NormalX=0 NormalY=0 NormalZ=1 AngleXU=0 Radius=1
    g62: BSplineCurve PolesCount=3 KnotsCount=2 Degree=2 IsPeriodic=0
    g63: GeomPoint X=125.607 Y=-21.7539 Z=0
    g64: GeomPoint X=127.325 Y=-24.2775 Z=0
    g65: Circle CenterX=302.996 CenterY=111.695 CenterZ=0 NormalX=0 NormalY=0 NormalZ=1 AngleXU=0 Radius=1
    g66: Circle CenterX=306.073 CenterY=114.251 CenterZ=0 NormalX=0 NormalY=0 NormalZ=1 AngleXU=0 Radius=1
    g67: Circle CenterX=306.073 CenterY=110.251 CenterZ=0 NormalX=0 NormalY=0 NormalZ=1 AngleXU=0 Radius=1
    g68: BSplineCurve PolesCount=3 KnotsCount=2 Degree=2 IsPeriodic=0
    g69: GeomPoint X=302.996 Y=111.695 Z=0
    g70: GeomPoint X=306.073 Y=110.251 Z=0
    g71: Circle CenterX=306.073 CenterY=95.2763 CenterZ=0 NormalX=0 NormalY=0 NormalZ=1 AngleXU=0 Radius=1
    g72: Circle CenterX=306.073 CenterY=91.2763 CenterZ=0 NormalX=0 NormalY=0 NormalZ=1 AngleXU=0 Radius=1
    g73: Circle CenterX=302.567 CenterY=89.3511 CenterZ=0 NormalX=0 NormalY=0 NormalZ=1 AngleXU=0 Radius=1
    g74: BSplineCurve PolesCount=3 KnotsCount=2 Degree=2 IsPeriodic=0
    g75: GeomPoint X=306.073 Y=95.2763 Z=0
    g76: GeomPoint X=302.567 Y=89.3511 Z=0
    g77: LineSegment StartX=306.073 StartY=110.251 StartZ=0 EndX=306.073 EndY=95.2763 EndZ=0
    g78: LineSegment StartX=302.996 StartY=111.695 StartZ=0 EndX=236.821 EndY=56.7187 EndZ=0
    g79: LineSegment StartX=238.538 StartY=54.1951 StartZ=0 EndX=302.567 EndY=89.3511 EndZ=0
    g80: Circle CenterX=61.1496 CenterY=111.695 CenterZ=0 NormalX=0 NormalY=0 NormalZ=1 AngleXU=0 Radius=1
    g81: Circle CenterX=58.0728 CenterY=114.251 CenterZ=0 NormalX=0 NormalY=0 NormalZ=1 AngleXU=0 Radius=1
    g82: Circle CenterX=58.0728 CenterY=110.251 CenterZ=0 NormalX=0 NormalY=0 NormalZ=1 AngleXU=0 Radius=1
    g83: BSplineCurve PolesCount=3 KnotsCount=2 Degree=2 IsPeriodic=0
    g84: GeomPoint X=61.1496 Y=111.695 Z=0
    g85: GeomPoint X=58.0728 Y=110.251 Z=0
    g86: Circle CenterX=61.5791 CenterY=89.3511 CenterZ=0 NormalX=0 NormalY=0 NormalZ=1 AngleXU=0 Radius=1
    g87: Circle CenterX=58.0728 CenterY=91.2763 CenterZ=0 NormalX=0 NormalY=0 NormalZ=1 AngleXU=0 Radius=1
    g88: Circle CenterX=58.0728 CenterY=95.2763 CenterZ=0 NormalX=0 NormalY=0 NormalZ=1 AngleXU=0 Radius=1
    g89: BSplineCurve PolesCount=3 KnotsCount=2 Degree=2 IsPeriodic=0
    g90: GeomPoint X=61.5791 Y=89.3511 Z=0
    g91: GeomPoint X=58.0728 Y=95.2763 Z=0
    g92: LineSegment StartX=58.0728 StartY=110.251 StartZ=0 EndX=58.0728 EndY=95.2763 EndZ=0
    g93: LineSegment StartX=61.1496 StartY=111.695 StartZ=0 EndX=127.326 EndY=56.7187 EndZ=0
    g94: LineSegment StartX=125.607 StartY=54.1951 StartZ=0 EndX=61.5791 EndY=89.3511 EndZ=0
    g95: Circle CenterX=61.5791 CenterY=-56.9099 CenterZ=0 NormalX=0 NormalY=0 NormalZ=1 AngleXU=0 Radius=1
    g96: Circle CenterX=58.0728 CenterY=-58.8351 CenterZ=0 NormalX=0 NormalY=0 NormalZ=1 AngleXU=0 Radius=1
    g97: Circle CenterX=58.0728 CenterY=-62.8351 CenterZ=0 NormalX=0 NormalY=0 NormalZ=1 AngleXU=0 Radius=1
    g98: BSplineCurve PolesCount=3 KnotsCount=2 Degree=2 IsPeriodic=0
    g99: GeomPoint X=61.5791 Y=-56.9099 Z=0
    g100: GeomPoint X=58.0728 Y=-62.8351 Z=0
    g101: Circle CenterX=58.0728 CenterY=-77.8102 CenterZ=0 NormalX=0 NormalY=0 NormalZ=1 AngleXU=0 Radius=1
    g102: Circle CenterX=58.0728 CenterY=-81.8102 CenterZ=0 NormalX=0 NormalY=0 NormalZ=1 AngleXU=0 Radius=1
    g103: Circle CenterX=61.1496 CenterY=-79.2541 CenterZ=0 NormalX=0 NormalY=0 NormalZ=1 AngleXU=0 Radius=1
    g104: BSplineCurve PolesCount=3 KnotsCount=2 Degree=2 IsPeriodic=0
    g105: GeomPoint X=58.0728 Y=-77.8102 Z=0
    g106: GeomPoint X=61.1496 Y=-79.2541 Z=0
    g107: LineSegment StartX=58.0728 StartY=-62.8351 StartZ=0 EndX=58.0728 EndY=-77.8102 EndZ=0
    g108: LineSegment StartX=61.1496 StartY=-79.2541 StartZ=0 EndX=127.325 EndY=-24.2775 EndZ=0
    g109: LineSegment StartX=125.607 StartY=-21.7539 StartZ=0 EndX=61.5791 EndY=-56.9099 EndZ=0
    g110: Circle CenterX=302.567 CenterY=-56.9099 CenterZ=0 NormalX=0 NormalY=0 NormalZ=1 AngleXU=0 Radius=1
    g111: Circle CenterX=306.073 CenterY=-58.8351 CenterZ=0 NormalX=0 NormalY=0 NormalZ=1 AngleXU=0 Radius=1
    g112: Circle CenterX=306.073 CenterY=-62.8351 CenterZ=0 NormalX=0 NormalY=0 NormalZ=1 AngleXU=0 Radius=1
    g113: BSplineCurve PolesCount=3 KnotsCount=2 Degree=2 IsPeriodic=0
    g114: GeomPoint X=302.567 Y=-56.9099 Z=0
    g115: GeomPoint X=306.073 Y=-62.8351 Z=0
    g116: Circle CenterX=302.996 CenterY=-79.2541 CenterZ=0 NormalX=0 NormalY=0 NormalZ=1 AngleXU=0 Radius=1
    g117: Circle CenterX=306.073 CenterY=-81.8102 CenterZ=0 NormalX=0 NormalY=0 NormalZ=1 AngleXU=0 Radius=1
    g118: Circle CenterX=306.073 CenterY=-77.8102 CenterZ=0 NormalX=0 NormalY=0 NormalZ=1 AngleXU=0 Radius=1
    g119: BSplineCurve PolesCount=3 KnotsCount=2 Degree=2 IsPeriodic=0
    g120: GeomPoint X=302.996 Y=-79.2541 Z=0
    g121: GeomPoint X=306.073 Y=-77.8102 Z=0
    g122: LineSegment StartX=306.073 StartY=-62.8351 StartZ=0 EndX=306.073 EndY=-77.8102 EndZ=0
    g123: LineSegment StartX=302.996 StartY=-79.2541 StartZ=0 EndX=236.821 EndY=-24.2775 EndZ=0
    g124: LineSegment StartX=238.538 StartY=-21.7539 StartZ=0 EndX=302.567 EndY=-56.9099 EndZ=0
    g125: Circle CenterX=61.6457 CenterY=-88.8112 CenterZ=0 NormalX=0 NormalY=0 NormalZ=1 AngleXU=0 Radius=1
    g126: Circle CenterX=58.0728 CenterY=-91.7794 CenterZ=0 NormalX=0 NormalY=0 NormalZ=1 AngleXU=0 Radius=1
    g127: Circle CenterX=63.9135 CenterY=-91.7791 CenterZ=0 NormalX=0 NormalY=0 NormalZ=1 AngleXU=0 Radius=1
    g128: BSplineCurve PolesCount=3 KnotsCount=2 Degree=2 IsPeriodic=0
    g129: GeomPoint X=61.6457 Y=-88.8112 Z=0
    g130: GeomPoint X=63.9135 Y=-91.7791 Z=0
    g131: Circle CenterX=179.022 CenterY=-85.8163 CenterZ=0 NormalX=0 NormalY=0 NormalZ=1 AngleXU=0 Radius=1
    g132: Circle CenterX=179.022 CenterY=-91.7794 CenterZ=0 NormalX=0 NormalY=0 NormalZ=1 AngleXU=0 Radius=1
    g133: Circle CenterX=171.895 CenterY=-91.7791 CenterZ=0 NormalX=0 NormalY=0 NormalZ=1 AngleXU=0 Radius=1
    g134: BSplineCurve PolesCount=3 KnotsCount=2 Degree=2 IsPeriodic=0
    g135: GeomPoint X=179.022 Y=-85.8163 Z=0
    g136: GeomPoint X=171.895 Y=-91.7791 Z=0
    g137: Circle CenterX=185.124 CenterY=-86.2028 CenterZ=0 NormalX=0 NormalY=0 NormalZ=1 AngleXU=0 Radius=1
    g138: Circle CenterX=185.124 CenterY=-91.7794 CenterZ=0 NormalX=0 NormalY=0 NormalZ=1 AngleXU=0 Radius=1
    g139: Circle CenterX=191.747 CenterY=-91.7794 CenterZ=0 NormalX=0 NormalY=0 NormalZ=1 AngleXU=0 Radius=1
    g140: BSplineCurve PolesCount=3 KnotsCount=2 Degree=2 IsPeriodic=0
    g141: GeomPoint X=185.124 Y=-86.2028 Z=0
    g142: GeomPoint X=191.747 Y=-91.7794 Z=0
    g143: Circle CenterX=299.888 CenterY=-86.6413 CenterZ=0 NormalX=0 NormalY=0 NormalZ=1 AngleXU=0 Radius=1
    g144: Circle CenterX=306.073 CenterY=-91.7794 CenterZ=0 NormalX=0 NormalY=0 NormalZ=1 AngleXU=0 Radius=1
    g145: Circle CenterX=298.776 CenterY=-91.7794 CenterZ=0 NormalX=0 NormalY=0 NormalZ=1 AngleXU=0 Radius=1
    g146: BSplineCurve PolesCount=3 KnotsCount=2 Degree=2 IsPeriodic=0
    g147: GeomPoint X=299.888 Y=-86.6413 Z=0
    g148: GeomPoint X=298.776 Y=-91.7794 Z=0
    g149: LineSegment StartX=189.124 StartY=5.37834 StartZ=0 EndX=299.888 EndY=-86.6413 EndZ=0
    g150: LineSegment StartX=298.776 StartY=-91.7794 StartZ=0 EndX=191.747 EndY=-91.7794 EndZ=0
    g151: LineSegment StartX=185.124 StartY=-86.2028 StartZ=0 EndX=185.124 EndY=5.34704 EndZ=0
    g152: LineSegment StartX=179.022 StartY=5.34704 StartZ=0 EndX=179.022 EndY=-85.8163 EndZ=0
    g153: LineSegment StartX=171.895 StartY=-91.7791 StartZ=0 EndX=63.9135 EndY=-91.7791 EndZ=0
    g154: LineSegment StartX=61.6457 StartY=-88.8112 StartZ=0 EndX=175.022 EndY=5.37834 EndZ=0
    g155: Circle CenterX=302.073 CenterY=124.221 CenterZ=0 NormalX=0 NormalY=0 NormalZ=1 AngleXU=0 Radius=1
    g156: Circle CenterX=306.073 CenterY=124.221 CenterZ=0 NormalX=0 NormalY=0 NormalZ=1 AngleXU=0 Radius=1
    g157: Circle CenterX=302.996 CenterY=121.665 CenterZ=0 NormalX=0 NormalY=0 NormalZ=1 AngleXU=0 Radius=1
    g158: BSplineCurve PolesCount=3 KnotsCount=2 Degree=2 IsPeriodic=0
    g159: GeomPoint X=302.073 Y=124.221 Z=0
    g160: GeomPoint X=302.996 Y=121.665 Z=0
    g161: Circle CenterX=189.124 CenterY=124.221 CenterZ=0 NormalX=0 NormalY=0 NormalZ=1 AngleXU=0 Radius=1
    g162: Circle CenterX=185.124 CenterY=124.221 CenterZ=0 NormalX=0 NormalY=0 NormalZ=1 AngleXU=0 Radius=1
    g163: Circle CenterX=185.124 CenterY=120.221 CenterZ=0 NormalX=0 NormalY=0 NormalZ=1 AngleXU=0 Radius=1
    g164: BSplineCurve PolesCount=3 KnotsCount=2 Degree=2 IsPeriodic=0
    g165: GeomPoint X=189.124 Y=124.221 Z=0
    g166: GeomPoint X=185.124 Y=120.221 Z=0
    g167: Circle CenterX=175.022 CenterY=124.221 CenterZ=0 NormalX=0 NormalY=0 NormalZ=1 AngleXU=0 Radius=1
    g168: Circle CenterX=179.022 CenterY=124.221 CenterZ=0 NormalX=0 NormalY=0 NormalZ=1 AngleXU=0 Radius=1
    g169: Circle CenterX=179.022 CenterY=120.221 CenterZ=0 NormalX=0 NormalY=0 NormalZ=1 AngleXU=0 Radius=1
    g170: BSplineCurve PolesCount=3 KnotsCount=2 Degree=2 IsPeriodic=0
    g171: GeomPoint X=175.022 Y=124.221 Z=0
    g172: GeomPoint X=179.022 Y=120.221 Z=0
    g173: Circle CenterX=62.0728 CenterY=124.221 CenterZ=0 NormalX=0 NormalY=0 NormalZ=1 AngleXU=0 Radius=1
    g174: Circle CenterX=58.0728 CenterY=124.221 CenterZ=0 NormalX=0 NormalY=0 NormalZ=1 AngleXU=0 Radius=1
    g175: Circle CenterX=61.1496 CenterY=121.665 CenterZ=0 NormalX=0 NormalY=0 NormalZ=1 AngleXU=0 Radius=1
    g176: BSplineCurve PolesCount=3 KnotsCount=2 Degree=2 IsPeriodic=0
    g177: GeomPoint X=62.0728 Y=124.221 Z=0
    g178: GeomPoint X=61.1496 Y=121.665 Z=0
    g179: LineSegment StartX=179.022 StartY=120.221 StartZ=0 EndX=179.022 EndY=27.0628 EndZ=0
    g180: LineSegment StartX=185.124 StartY=27.0628 StartZ=0 EndX=185.124 EndY=120.221 EndZ=0
    g181: LineSegment StartX=302.996 StartY=121.665 StartZ=0 EndX=189.124 EndY=27.0628 EndZ=0
    g182: LineSegment StartX=175.022 StartY=27.0628 StartZ=0 EndX=61.1496 EndY=121.665 EndZ=0
    g183: Circle CenterX=61.5791 CenterY=75.4095 CenterZ=0 NormalX=0 NormalY=0 NormalZ=1 AngleXU=0 Radius=1
    g184: Circle CenterX=58.0728 CenterY=77.3346 CenterZ=0 NormalX=0 NormalY=0 NormalZ=1 AngleXU=0 Radius=1
    g185: Circle CenterX=58.0728 CenterY=73.3346 CenterZ=0 NormalX=0 NormalY=0 NormalZ=1 AngleXU=0 Radius=1
    g186: BSplineCurve PolesCount=3 KnotsCount=2 Degree=2 IsPeriodic=0
    g187: GeomPoint X=61.5791 Y=75.4095 Z=0
    g188: GeomPoint X=58.0728 Y=73.3346 Z=0
    g189: Circle CenterX=58.0728 CenterY=-40.8935 CenterZ=0 NormalX=0 NormalY=0 NormalZ=1 AngleXU=0 Radius=1
    g190: Circle CenterX=58.0728 CenterY=-44.8935 CenterZ=0 NormalX=0 NormalY=0 NormalZ=1 AngleXU=0 Radius=1
    g191: Circle CenterX=61.5791 CenterY=-42.9683 CenterZ=0 NormalX=0 NormalY=0 NormalZ=1 AngleXU=0 Radius=1
    g192: BSplineCurve PolesCount=3 KnotsCount=2 Degree=2 IsPeriodic=0
    g193: GeomPoint X=58.0728 Y=-40.8935 Z=0
    g194: GeomPoint X=61.5791 Y=-42.9683 Z=0
    g195: LineSegment StartX=61.5791 StartY=-42.9683 StartZ=0 EndX=165.871 EndY=14.2954 EndZ=0
    g196: LineSegment StartX=165.871 StartY=18.1458 StartZ=0 EndX=61.5791 EndY=75.4095 EndZ=0
    g197: LineSegment StartX=58.0728 StartY=73.3346 StartZ=0 EndX=58.0728 EndY=-40.8935 EndZ=0
    g198: Circle CenterX=302.567 CenterY=-42.9683 CenterZ=0 NormalX=0 NormalY=0 NormalZ=1 AngleXU=0 Radius=1
    g199: Circle CenterX=306.073 CenterY=-44.8935 CenterZ=0 NormalX=0 NormalY=0 NormalZ=1 AngleXU=0 Radius=1
    g200: Circle CenterX=306.073 CenterY=-40.8935 CenterZ=0 NormalX=0 NormalY=0 NormalZ=1 AngleXU=0 Radius=1
    g201: BSplineCurve PolesCount=3 KnotsCount=2 Degree=2 IsPeriodic=0
    g202: GeomPoint X=302.567 Y=-42.9683 Z=0
    g203: GeomPoint X=306.073 Y=-40.8935 Z=0
    g204: Circle CenterX=306.073 CenterY=73.3346 CenterZ=0 NormalX=0 NormalY=0 NormalZ=1 AngleXU=0 Radius=1
    g205: Circle CenterX=306.073 CenterY=77.3346 CenterZ=0 NormalX=0 NormalY=0 NormalZ=1 AngleXU=0 Radius=1
    g206: Circle CenterX=302.567 CenterY=75.4095 CenterZ=0 NormalX=0 NormalY=0 NormalZ=1 AngleXU=0 Radius=1
    g207: BSplineCurve PolesCount=3 KnotsCount=2 Degree=2 IsPeriodic=0
    g208: GeomPoint X=306.073 Y=73.3346 Z=0
    g209: GeomPoint X=302.567 Y=75.4095 Z=0
    g210: LineSegment StartX=302.567 StartY=-42.9683 StartZ=0 EndX=198.275 EndY=14.2954 EndZ=0
    g211: LineSegment StartX=198.275 StartY=18.1458 StartZ=0 EndX=302.567 EndY=75.4095 EndZ=0
    g212: LineSegment StartX=306.073 StartY=73.3346 StartZ=0 EndX=306.073 EndY=-40.8935 EndZ=0
    g213: LineSegment StartX=322.073 StartY=105.865 StartZ=0 EndX=328.643 EndY=105.865 EndZ=0
    g214: LineSegment StartX=318.073 StartY=120.221 StartZ=0 EndX=318.073 EndY=109.865 EndZ=0
    g215: LineSegment StartX=336.157 StartY=107.779 StartZ=0 EndX=362.567 EndY=122.294 EndZ=0
    g216: Circle CenterX=362.073 CenterY=124.221 CenterZ=0 NormalX=0 NormalY=0 NormalZ=1 AngleXU=0 Radius=1
    g217: Circle CenterX=366.073 CenterY=124.221 CenterZ=0 NormalX=0 NormalY=0 NormalZ=1 AngleXU=0 Radius=1
    g218: Circle CenterX=362.567 CenterY=122.294 CenterZ=0 NormalX=0 NormalY=0 NormalZ=1 AngleXU=0 Radius=1
    g219: BSplineCurve PolesCount=3 KnotsCount=2 Degree=2 IsPeriodic=0
    g220: GeomPoint X=362.073 Y=124.221 Z=0
    g221: GeomPoint X=362.567 Y=122.294 Z=0
    g222: Circle CenterX=322.073 CenterY=124.221 CenterZ=0 NormalX=0 NormalY=0 NormalZ=1 AngleXU=0 Radius=1
    g223: Circle CenterX=318.073 CenterY=124.221 CenterZ=0 NormalX=0 NormalY=0 NormalZ=1 AngleXU=0 Radius=1
    g224: Circle CenterX=318.073 CenterY=120.221 CenterZ=0 NormalX=0 NormalY=0 NormalZ=1 AngleXU=0 Radius=1
    g225: BSplineCurve PolesCount=3 KnotsCount=2 Degree=2 IsPeriodic=0
    g226: GeomPoint X=322.073 Y=124.221 Z=0
    g227: GeomPoint X=318.073 Y=120.221 Z=0
    g228: Circle CenterX=322.073 CenterY=105.865 CenterZ=0 NormalX=0 NormalY=0 NormalZ=1 AngleXU=0 Radius=1
    g229: Circle CenterX=318.073 CenterY=105.865 CenterZ=0 NormalX=0 NormalY=0 NormalZ=1 AngleXU=0 Radius=1
    g230: Circle CenterX=318.073 CenterY=109.865 CenterZ=0 NormalX=0 NormalY=0 NormalZ=1 AngleXU=0 Radius=1
    g231: BSplineCurve PolesCount=3 KnotsCount=2 Degree=2 IsPeriodic=0
    g232: GeomPoint X=322.073 Y=105.865 Z=0
    g233: GeomPoint X=318.073 Y=109.865 Z=0
    g234: Circle CenterX=336.157 CenterY=107.779 CenterZ=0 NormalX=0 NormalY=0 NormalZ=1 AngleXU=0 Radius=1
    g235: Circle CenterX=332.651 CenterY=105.853 CenterZ=0 NormalX=0 NormalY=0 NormalZ=1 AngleXU=0 Radius=1
    g236: Circle CenterX=328.643 CenterY=105.865 CenterZ=0 NormalX=0 NormalY=0 NormalZ=1 AngleXU=0 Radius=1
    g237: BSplineCurve PolesCount=3 KnotsCount=2 Degree=2 IsPeriodic=0
    g238: GeomPoint X=336.157 Y=107.779 Z=0
    g239: GeomPoint X=328.643 Y=105.865 Z=0
    g240: LineSegment StartX=322.073 StartY=124.221 StartZ=0 EndX=362.073 EndY=124.221 EndZ=0
    g241: Circle CenterX=371.567 CenterY=-80.8644 CenterZ=0 NormalX=0 NormalY=0 NormalZ=1 AngleXU=0 Radius=1
    g242: Circle CenterX=375.073 CenterY=-82.7896 CenterZ=0 NormalX=0 NormalY=0 NormalZ=1 AngleXU=0 Radius=1
    g243: Circle CenterX=375.073 CenterY=-78.7896 CenterZ=0 NormalX=0 NormalY=0 NormalZ=1 AngleXU=0 Radius=1
    g244: BSplineCurve PolesCount=3 KnotsCount=2 Degree=2 IsPeriodic=0
    g245: GeomPoint X=371.567 Y=-80.8644 Z=0
    g246: GeomPoint X=375.073 Y=-78.7896 Z=0
    g247: Circle CenterX=321.579 CenterY=-53.4075 CenterZ=0 NormalX=0 NormalY=0 NormalZ=1 AngleXU=0 Radius=1
    g248: Circle CenterX=318.073 CenterY=-51.4823 CenterZ=0 NormalX=0 NormalY=0 NormalZ=1 AngleXU=0 Radius=1
    g249: Circle CenterX=318.073 CenterY=-47.4805 CenterZ=0 NormalX=0 NormalY=0 NormalZ=1 AngleXU=0 Radius=1
    g250: BSplineCurve PolesCount=3 KnotsCount=2 Degree=2 IsPeriodic=0
    g251: GeomPoint X=321.579 Y=-53.4075 Z=0
    g252: GeomPoint X=318.073 Y=-47.4805 Z=0
    g253: LineSegment StartX=371.567 StartY=-80.8644 StartZ=0 EndX=321.579 EndY=-53.4075 EndZ=0
    g254: Circle CenterX=321.579 CenterY=-67.3492 CenterZ=0 NormalX=0 NormalY=0 NormalZ=1 AngleXU=0 Radius=1
    g255: Circle CenterX=318.073 CenterY=-65.424 CenterZ=0 NormalX=0 NormalY=0 NormalZ=1 AngleXU=0 Radius=1
    g256: Circle CenterX=318.073 CenterY=-69.424 CenterZ=0 NormalX=0 NormalY=0 NormalZ=1 AngleXU=0 Radius=1
    g257: BSplineCurve PolesCount=3 KnotsCount=2 Degree=2 IsPeriodic=0
    g258: GeomPoint X=321.579 Y=-67.3492 Z=0
    g259: GeomPoint X=318.073 Y=-69.424 Z=0
    g260: Circle CenterX=362.567 CenterY=-89.8542 CenterZ=0 NormalX=0 NormalY=0 NormalZ=1 AngleXU=0 Radius=1
    g261: Circle CenterX=366.073 CenterY=-91.7794 CenterZ=0 NormalX=0 NormalY=0 NormalZ=1 AngleXU=0 Radius=1
    g262: Circle CenterX=362.073 CenterY=-91.7794 CenterZ=0 NormalX=0 NormalY=0 NormalZ=1 AngleXU=0 Radius=1
    g263: BSplineCurve PolesCount=3 KnotsCount=2 Degree=2 IsPeriodic=0
    g264: GeomPoint X=362.567 Y=-89.8542 Z=0
    g265: GeomPoint X=362.073 Y=-91.7794 Z=0
    g266: Circle CenterX=322.073 CenterY=-91.7794 CenterZ=0 NormalX=0 NormalY=0 NormalZ=1 AngleXU=0 Radius=1
    g267: Circle CenterX=318.073 CenterY=-91.7794 CenterZ=0 NormalX=0 NormalY=0 NormalZ=1 AngleXU=0 Radius=1
    g268: Circle CenterX=318.073 CenterY=-87.7794 CenterZ=0 NormalX=0 NormalY=0 NormalZ=1 AngleXU=0 Radius=1
    g269: BSplineCurve PolesCount=3 KnotsCount=2 Degree=2 IsPeriodic=0
    g270: GeomPoint X=322.073 Y=-91.7794 Z=0
    g271: GeomPoint X=318.073 Y=-87.7794 Z=0
    g272: LineSegment StartX=362.567 StartY=-89.8542 StartZ=0 EndX=321.579 EndY=-67.3492 EndZ=0
    g273: LineSegment StartX=318.073 StartY=-69.424 StartZ=0 EndX=318.073 EndY=-87.7794 EndZ=0
    g274: LineSegment StartX=322.073 StartY=-91.7794 StartZ=0 EndX=362.073 EndY=-91.7794 EndZ=0
    g275: Circle CenterX=2.07281 CenterY=124.221 CenterZ=0 NormalX=0 NormalY=0 NormalZ=1 AngleXU=0 Radius=1
    g276: Circle CenterX=1.57905 CenterY=122.295 CenterZ=0 NormalX=0 NormalY=0 NormalZ=1 AngleXU=0 Radius=1
    g277: BSplineCurve PolesCount=3 KnotsCount=2 Degree=2 IsPeriodic=0
    g278: GeomPoint X=2.07281 Y=124.221 Z=0
    g279: GeomPoint X=1.57905 Y=122.295 Z=0
    g280: Circle CenterX=42.0728 CenterY=124.221 CenterZ=0 NormalX=0 NormalY=0 NormalZ=1 AngleXU=0 Radius=1
    g281: Circle CenterX=46.0728 CenterY=124.221 CenterZ=0 NormalX=0 NormalY=0 NormalZ=1 AngleXU=0 Radius=1
    g282: Circle CenterX=46.0728 CenterY=120.221 CenterZ=0 NormalX=0 NormalY=0 NormalZ=1 AngleXU=0 Radius=1
    g283: BSplineCurve PolesCount=3 KnotsCount=2 Degree=2 IsPeriodic=0
    g284: GeomPoint X=42.0728 Y=124.221 Z=0
    g285: GeomPoint X=46.0728 Y=120.221 Z=0
    g286: Circle CenterX=46.0728 CenterY=109.865 CenterZ=0 NormalX=0 NormalY=0 NormalZ=1 AngleXU=0 Radius=1
    g287: Circle CenterX=46.0728 CenterY=105.865 CenterZ=0 NormalX=0 NormalY=0 NormalZ=1 AngleXU=0 Radius=1
    g288: Circle CenterX=42.0728 CenterY=105.865 CenterZ=0 NormalX=0 NormalY=0 NormalZ=1 AngleXU=0 Radius=1
    g289: BSplineCurve PolesCount=3 KnotsCount=2 Degree=2 IsPeriodic=0
    g290: GeomPoint X=46.0728 Y=109.865 Z=0
    g291: GeomPoint X=42.0728 Y=105.865 Z=0
    g292: Circle CenterX=35.5028 CenterY=105.865 CenterZ=0 NormalX=0 NormalY=0 NormalZ=1 AngleXU=0 Radius=1
    g293: Circle CenterX=31.5028 CenterY=105.865 CenterZ=0 NormalX=0 NormalY=0 NormalZ=1 AngleXU=0 Radius=1
    g294: Circle CenterX=27.9965 CenterY=107.79 CenterZ=0 NormalX=0 NormalY=0 NormalZ=1 AngleXU=0 Radius=1
    g295: BSplineCurve PolesCount=3 KnotsCount=2 Degree=2 IsPeriodic=0
    g296: GeomPoint X=35.5028 Y=105.865 Z=0
    g297: GeomPoint X=27.9965 Y=107.79 Z=0
    g298: LineSegment StartX=2.07281 StartY=124.221 StartZ=0 EndX=42.0728 EndY=124.221 EndZ=0
    g299: LineSegment StartX=46.0728 StartY=120.221 StartZ=0 EndX=46.0728 EndY=109.865 EndZ=0
    g300: LineSegment StartX=42.0728 StartY=105.865 StartZ=0 EndX=35.5028 EndY=105.865 EndZ=0
    g301: LineSegment StartX=27.9965 StartY=107.79 StartZ=0 EndX=1.57905 EndY=122.295 EndZ=0
    g302: Circle CenterX=42.5666 CenterY=-67.3492 CenterZ=0 NormalX=0 NormalY=0 NormalZ=1 AngleXU=0 Radius=1
    g303: Circle CenterX=46.0728 CenterY=-65.424 CenterZ=0 NormalX=0 NormalY=0 NormalZ=1 AngleXU=0 Radius=1
    g304: Circle CenterX=46.0728 CenterY=-69.424 CenterZ=0 NormalX=0 NormalY=0 NormalZ=1 AngleXU=0 Radius=1
    g305: BSplineCurve PolesCount=3 KnotsCount=2 Degree=2 IsPeriodic=0
    g306: GeomPoint X=42.5666 Y=-67.3492 Z=0
    g307: GeomPoint X=46.0728 Y=-69.424 Z=0
    g308: Circle CenterX=46.0728 CenterY=-87.7794 CenterZ=0 NormalX=0 NormalY=0 NormalZ=1 AngleXU=0 Radius=1
    g309: Circle CenterX=46.0728 CenterY=-91.7794 CenterZ=0 NormalX=0 NormalY=0 NormalZ=1 AngleXU=0 Radius=1
    g310: Circle CenterX=42.0728 CenterY=-91.7794 CenterZ=0 NormalX=0 NormalY=0 NormalZ=1 AngleXU=0 Radius=1
    g311: BSplineCurve PolesCount=3 KnotsCount=2 Degree=2 IsPeriodic=0
    g312: GeomPoint X=46.0728 Y=-87.7794 Z=0
    g313: GeomPoint X=42.0728 Y=-91.7794 Z=0
    g314: Circle CenterX=2.07281 CenterY=-91.7794 CenterZ=0 NormalX=0 NormalY=0 NormalZ=1 AngleXU=0 Radius=1
    g315: Circle CenterX=-1.92719 CenterY=-91.7794 CenterZ=0 NormalX=0 NormalY=0 NormalZ=1 AngleXU=0 Radius=1
    g316: Circle CenterX=1.57905 CenterY=-89.8542 CenterZ=0 NormalX=0 NormalY=0 NormalZ=1 AngleXU=0 Radius=1
    g317: BSplineCurve PolesCount=3 KnotsCount=2 Degree=2 IsPeriodic=0
    g318: GeomPoint X=2.07281 Y=-91.7794 Z=0
    g319: GeomPoint X=1.57905 Y=-89.8542 Z=0
    g320: LineSegment StartX=2.07281 StartY=-91.7794 StartZ=0 EndX=42.0728 EndY=-91.7794 EndZ=0
    g321: LineSegment StartX=46.0728 StartY=-87.7794 StartZ=0 EndX=46.0728 EndY=-69.424 EndZ=0
    g322: LineSegment StartX=42.5666 StartY=-67.3492 StartZ=0 EndX=1.57905 EndY=-89.8542 EndZ=0
    g323: Circle CenterX=322.073 CenterY=76.4095 CenterZ=0 NormalX=0 NormalY=0 NormalZ=1 AngleXU=0 Radius=4
    g324: BSplineCurve PolesCount=3 KnotsCount=2 Degree=2 IsPeriodic=0
    g325: GeomPoint X=318.073 Y=72.4095 Z=0
    g326: GeomPoint X=322.073 Y=76.4095 Z=0
    g327: Circle CenterX=375.073 CenterY=72.4095 CenterZ=0 NormalX=0 NormalY=0 NormalZ=1 AngleXU=0 Radius=1
    g328: Circle CenterX=375.073 CenterY=76.4095 CenterZ=0 NormalX=0 NormalY=0 NormalZ=1 AngleXU=0 Radius=1
    g329: Circle CenterX=371.073 CenterY=76.4095 CenterZ=0 NormalX=0 NormalY=0 NormalZ=1 AngleXU=0 Radius=1
    g330: BSplineCurve PolesCount=3 KnotsCount=2 Degree=2 IsPeriodic=0
    g331: GeomPoint X=375.073 Y=72.4095 Z=0
    g332: GeomPoint X=371.073 Y=76.4095 Z=0
    g333: LineSegment StartX=322.073 StartY=76.4095 StartZ=0 EndX=371.073 EndY=76.4095 EndZ=0
    g334: LineSegment StartX=318.073 StartY=72.4095 StartZ=0 EndX=318.073 EndY=-47.4805 EndZ=0
    g335: LineSegment StartX=375.073 StartY=72.4095 StartZ=0 EndX=375.073 EndY=-78.7896 EndZ=0
    g336: ArcOfCircle CenterX=-26.9272 CenterY=22.1087 CenterZ=0 NormalX=0 NormalY=0 NormalZ=1 AngleXU=0 Radius=4 StartAngle=5e-16 EndAngle=3.14159
    g337: LineSegment StartX=-22.9272 StartY=22.1087 StartZ=0 EndX=-18.9272 EndY=-83.7794 EndZ=0
    g338: LineSegment StartX=-34.9272 StartY=-83.7794 StartZ=0 EndX=-30.9272 EndY=22.1087 EndZ=0
    g339: ArcOfCircle CenterX=391.073 CenterY=22.1087 CenterZ=0 NormalX=0 NormalY=0 NormalZ=1 AngleXU=0 Radius=4 StartAngle=0 EndAngle=3.14159
    g340: LineSegment StartX=387.073 StartY=22.1087 StartZ=0 EndX=383.073 EndY=-83.7794 EndZ=0
    g341: LineSegment StartX=395.073 StartY=22.1087 StartZ=0 EndX=399.073 EndY=-83.7794 EndZ=0
    g342: Circle CenterX=-10.9272 CenterY=-78.7794 CenterZ=0 NormalX=0 NormalY=0 NormalZ=1 AngleXU=0 Radius=1
    g343: Circle CenterX=-10.9272 CenterY=-82.7794 CenterZ=0 NormalX=0 NormalY=0 NormalZ=1 AngleXU=0 Radius=1
    g344: Circle CenterX=-7.42095 CenterY=-80.8542 CenterZ=0 NormalX=0 NormalY=0 NormalZ=1 AngleXU=0 Radius=1
    g345: BSplineCurve PolesCount=3 KnotsCount=2 Degree=2 IsPeriodic=0
    g346: GeomPoint X=-10.9272 Y=-78.7794 Z=0
    g347: GeomPoint X=-7.42095 Y=-80.8542 Z=0
    g348: Circle CenterX=42.5666 CenterY=-53.4075 CenterZ=0 NormalX=0 NormalY=0 NormalZ=1 AngleXU=0 Radius=1
    g349: Circle CenterX=46.0728 CenterY=-51.4823 CenterZ=0 NormalX=0 NormalY=0 NormalZ=1 AngleXU=0 Radius=1
    g350: Circle CenterX=46.0728 CenterY=-47.4823 CenterZ=0 NormalX=0 NormalY=0 NormalZ=1 AngleXU=0 Radius=1
    g351: BSplineCurve PolesCount=3 KnotsCount=2 Degree=2 IsPeriodic=0
    g352: GeomPoint X=42.5666 Y=-53.4075 Z=0
    g353: GeomPoint X=46.0728 Y=-47.4823 Z=0
    g354: Circle CenterX=46.0728 CenterY=72.4095 CenterZ=0 NormalX=0 NormalY=0 NormalZ=1 AngleXU=0 Radius=1
    g355: Circle CenterX=46.0728 CenterY=76.4095 CenterZ=0 NormalX=0 NormalY=0 NormalZ=1 AngleXU=0 Radius=1
    g356: Circle CenterX=42.0728 CenterY=76.4095 CenterZ=0 NormalX=0 NormalY=0 NormalZ=1 AngleXU=0 Radius=1
    g357: BSplineCurve PolesCount=3 KnotsCount=2 Degree=2 IsPeriodic=0
    g358: GeomPoint X=46.0728 Y=72.4095 Z=0
    g359: GeomPoint X=42.0728 Y=76.4095 Z=0
    g360: Circle CenterX=-6.92718 CenterY=76.4095 CenterZ=0 NormalX=0 NormalY=0 NormalZ=1 AngleXU=0 Radius=1
    g361: Circle CenterX=-10.9272 CenterY=76.4095 CenterZ=0 NormalX=0 NormalY=0 NormalZ=1 AngleXU=0 Radius=1
    g362: Circle CenterX=-10.9272 CenterY=72.4095 CenterZ=0 NormalX=0 NormalY=0 NormalZ=1 AngleXU=0 Radius=1
    g363: BSplineCurve PolesCount=3 KnotsCount=2 Degree=2 IsPeriodic=0
    g364: GeomPoint X=-6.92718 Y=76.4095 Z=0
    g365: GeomPoint X=-10.9272 Y=72.4095 Z=0
    g366: LineSegment StartX=-10.9272 StartY=72.4095 StartZ=0 EndX=-10.9272 EndY=-78.7794 EndZ=0
    g367: LineSegment StartX=-7.42095 StartY=-80.8542 StartZ=0 EndX=42.5666 EndY=-53.4075 EndZ=0
    g368: LineSegment StartX=46.0728 StartY=-47.4823 StartZ=0 EndX=46.0728 EndY=72.4095 EndZ=0
    g369: LineSegment StartX=42.0728 StartY=76.4095 StartZ=0 EndX=-6.92719 EndY=76.4095 EndZ=0
    g370: LineSegment StartX=119.072 StartY=136.221 StartZ=0 EndX=119.072 EndY=-116.228 EndZ=0
    g371: LineSegment StartX=-42.9272 StartY=136.221 StartZ=0 EndX=407.073 EndY=136.221 EndZ=0
    g372: LineSegment StartX=232.072 StartY=136.221 StartZ=0 EndX=220.072 EndY=136.221 EndZ=0
    g373: LineSegment StartX=232.072 StartY=136.221 StartZ=0 EndX=232.072 EndY=124.221 EndZ=0
    g374: LineSegment StartX=220.072 StartY=136.221 StartZ=0 EndX=220.072 EndY=124.221 EndZ=0
    g375: LineSegment StartX=220.072 StartY=136.221 StartZ=0 EndX=226.072 EndY=136.221 EndZ=0
    g376: LineSegment StartX=220.072 StartY=136.221 StartZ=0 EndX=220.072 EndY=130.221 EndZ=0
    g377: LineSegment StartX=220.072 StartY=124.221 StartZ=0 EndX=226.072 EndY=124.221 EndZ=0
    g378: LineSegment StartX=232.072 StartY=124.221 StartZ=0 EndX=232.072 EndY=127.221 EndZ=0
    g379: LineSegment StartX=232.072 StartY=136.221 StartZ=0 EndX=232.072 EndY=133.221 EndZ=0
    g380-g384: Circle x5 (B-spline internal-alignment scaffolding for g385; pole/knot coordinates omitted)
    g385: BSplineCurve PolesCount=5 KnotsCount=3 Degree=3 IsPeriodic=0
    g386: GeomPoint X=232.072 Y=133.221 Z=0
    g387: GeomPoint X=223.072 Y=130.221 Z=0
    g388: GeomPoint X=232.072 Y=127.221 Z=0
    g389: LineSegment StartX=189.124 StartY=124.221 StartZ=0 EndX=302.073 EndY=124.221 EndZ=0
    g390: LineSegment StartX=132.072 StartY=136.221 StartZ=0 EndX=132.072 EndY=124.221 EndZ=0
    g391: LineSegment StartX=132.072 StartY=136.221 StartZ=0 EndX=144.072 EndY=136.221 EndZ=0
    g392: LineSegment StartX=144.072 StartY=136.221 StartZ=0 EndX=144.072 EndY=124.221 EndZ=0
    g393: LineSegment StartX=144.072 StartY=136.221 StartZ=0 EndX=138.072 EndY=136.221 EndZ=0
    g394: LineSegment StartX=144.072 StartY=136.221 StartZ=0 EndX=144.072 EndY=130.221 EndZ=0
    g395: LineSegment StartX=132.072 StartY=136.221 StartZ=0 EndX=132.072 EndY=133.221 EndZ=0
    g396: LineSegment StartX=132.072 StartY=133.221 StartZ=0 EndX=132.072 EndY=127.221 EndZ=0
    g397-g401: Circle x5 (B-spline internal-alignment scaffolding for g402; pole/knot coordinates omitted)
    g402: BSplineCurve PolesCount=5 KnotsCount=3 Degree=3 IsPeriodic=0
    g403: GeomPoint X=132.072 Y=133.221 Z=0
    g404: GeomPoint X=141.072 Y=130.221 Z=0
    g405: GeomPoint X=132.072 Y=127.221 Z=0
    g406: LineSegment StartX=132.072 StartY=124.221 StartZ=0 EndX=175.022 EndY=124.221 EndZ=0
    g407: LineSegment StartX=62.0728 StartY=124.221 StartZ=0 EndX=132.072 EndY=124.221 EndZ=0
    ... +19 more geometry lines
  constraints (729):
    c: Vertical(g0)
    c: Vertical(g1)
    c: Block(g1)
    c: Block(g0)
    c: Weight(g4) = 1
    c: Equal(g4,g5)
    c: Equal(g4,g6)
    c: InternalAlignment(g4,g7)
    c: InternalAlignment(g5,g7)
    c: InternalAlignment(g6,g7)
    c: InternalAlignment(g8,g7)
    c: InternalAlignment(g9,g7)
    c: Weight(g10) = 1
    c: Equal(g10,g11)
    c: Equal(g10,g12)
    c: InternalAlignment(g10,g13)
    c: InternalAlignment(g11,g13)
    c: InternalAlignment(g12,g13)
    c: InternalAlignment(g14,g13)
    c: InternalAlignment(g15,g13)
    c: Block(g13)
    c: Block(g7)
    c: Weight(g16) = 1
    c: Equal(g16,g17)
    c: Equal(g16,g18)
    c: InternalAlignment(g16,g19)
    c: InternalAlignment(g17,g19)
    c: InternalAlignment(g18,g19)
    c: InternalAlignment(g20,g19)
    c: InternalAlignment(g21,g19)
    c: Weight(g22) = 1
    c: Equal(g22,g23)
    c: Equal(g22,g24)
    c: InternalAlignment(g22,g25)
    c: InternalAlignment(g23,g25)
    c: InternalAlignment(g24,g25)
    c: InternalAlignment(g26,g25)
    c: InternalAlignment(g27,g25)
    c: Block(g25)
    c: Block(g19)
    c: Weight(g28) = 1
    c: Equal(g28,g29)
    c: Equal(g28,g30)
    c: InternalAlignment(g28,g31)
    c: InternalAlignment(g29,g31)
    c: InternalAlignment(g30,g31)
    c: InternalAlignment(g32,g31)
    c: InternalAlignment(g33,g31)
    c: Weight(g34) = 1
    c: Equal(g34,g35)
    c: Equal(g34,g36)
    c: InternalAlignment(g34,g37)
    c: InternalAlignment(g35,g37)
    c: InternalAlignment(g36,g37)
    c: InternalAlignment(g38,g37)
    c: InternalAlignment(g39,g37)
    c: Block(g31)
    c: Block(g37)
    c: Coincident(g40,g1)
    c: Coincident(g40,g0)
    c: Horizontal(g40)
    c: Distance(g40) = 450
    c: Weight(g41) = 1
    c: Equal(g41,g42)
    c: Equal(g41,g43)
    c: InternalAlignment(g41,g44)
    c: InternalAlignment(g42,g44)
    c: InternalAlignment(g43,g44)
    c: InternalAlignment(g45,g44)
    c: InternalAlignment(g46,g44)
    c: Block(g44)
    c: Weight(g47) = 1
    c: Equal(g47,g48)
    c: Equal(g47,g49)
    c: InternalAlignment(g47,g50)
    c: InternalAlignment(g48,g50)
    c: InternalAlignment(g49,g50)
    c: InternalAlignment(g51,g50)
    c: InternalAlignment(g52,g50)
    c: Block(g50)
    c: Weight(g53) = 1
    c: Equal(g53,g54)
    c: Equal(g53,g55)
    c: InternalAlignment(g53,g56)
    c: InternalAlignment(g54,g56)
    c: InternalAlignment(g55,g56)
    c: InternalAlignment(g57,g56)
    c: InternalAlignment(g58,g56)
    c: Block(g56)
    c: Weight(g59) = 1
    c: Equal(g59,g60)
    c: Equal(g59,g61)
    c: InternalAlignment(g59,g62)
    c: InternalAlignment(g60,g62)
    c: InternalAlignment(g61,g62)
    c: InternalAlignment(g63,g62)
    c: InternalAlignment(g64,g62)
    c: Block(g62)
    c: Weight(g65) = 1
    c: Equal(g65,g66)
    c: Equal(g65,g67)
    c: InternalAlignment(g65,g68)
    c: InternalAlignment(g66,g68)
    c: InternalAlignment(g67,g68)
    c: InternalAlignment(g69,g68)
    c: InternalAlignment(g70,g68)
    c: Weight(g71) = 1
    c: Equal(g71,g72)
    c: Equal(g71,g73)
    c: InternalAlignment(g71,g74)
    c: InternalAlignment(g72,g74)
    c: InternalAlignment(g73,g74)
    c: InternalAlignment(g75,g74)
    c: InternalAlignment(g76,g74)
    c: Block(g68)
    c: Block(g74)
    c: Coincident(g77,g68)
    c: Coincident(g77,g74)
    c: Vertical(g77)
    c: Coincident(g78,g68)
    c: Coincident(g78,g50)
    c: Coincident(g79,g50)
    c: Coincident(g79,g74)
    c: Weight(g80) = 1
    c: Equal(g80,g81)
    c: Equal(g80,g82)
    c: InternalAlignment(g80,g83)
    c: InternalAlignment(g81,g83)
    c: InternalAlignment(g82,g83)
    c: InternalAlignment(g84,g83)
    c: InternalAlignment(g85,g83)
    c: Weight(g86) = 1
    c: Equal(g86,g87)
    c: Equal(g86,g88)
    c: InternalAlignment(g86,g89)
    c: InternalAlignment(g87,g89)
    c: InternalAlignment(g88,g89)
    c: InternalAlignment(g90,g89)
    c: InternalAlignment(g91,g89)
    c: Block(g83)
    c: Block(g89)
    c: Coincident(g92,g83)
    c: Coincident(g92,g89)
    c: Vertical(g92)
    c: Coincident(g93,g83)
    c: Coincident(g93,g44)
    c: Coincident(g94,g44)
    c: Coincident(g94,g89)
    c: Weight(g95) = 1
    c: Equal(g95,g96)
    c: Equal(g95,g97)
    c: InternalAlignment(g95,g98)
    c: InternalAlignment(g96,g98)
    c: InternalAlignment(g97,g98)
    c: InternalAlignment(g99,g98)
    c: InternalAlignment(g100,g98)
    c: Weight(g101) = 1
    c: Equal(g101,g102)
    c: Equal(g101,g103)
    c: InternalAlignment(g101,g104)
    c: InternalAlignment(g102,g104)
    c: InternalAlignment(g103,g104)
    c: InternalAlignment(g105,g104)
    c: InternalAlignment(g106,g104)
    c: Block(g98)
    c: Block(g104)
    c: Coincident(g107,g98)
    c: Coincident(g107,g104)
    c: Vertical(g107)
    c: Coincident(g108,g104)
    c: Coincident(g108,g62)
    c: Coincident(g109,g62)
    c: Coincident(g109,g98)
    c: Weight(g110) = 1
    c: Equal(g110,g111)
    c: Equal(g110,g112)
    c: InternalAlignment(g110,g113)
    c: InternalAlignment(g111,g113)
    c: InternalAlignment(g112,g113)
    c: InternalAlignment(g114,g113)
    c: InternalAlignment(g115,g113)
    c: Weight(g116) = 1
    c: Equal(g116,g117)
    c: Equal(g116,g118)
    c: InternalAlignment(g116,g119)
    c: InternalAlignment(g117,g119)
    c: InternalAlignment(g118,g119)
    c: InternalAlignment(g120,g119)
    c: InternalAlignment(g121,g119)
    c: Block(g113)
    c: Block(g119)
    c: Coincident(g122,g113)
    c: Coincident(g122,g119)
    c: Vertical(g122)
    c: Coincident(g123,g119)
    c: Coincident(g123,g56)
    c: Coincident(g124,g56)
    c: Coincident(g124,g113)
    c: Weight(g125) = 1
    c: Equal(g125,g126)
    c: Equal(g125,g127)
    c: InternalAlignment(g125,g128)
    c: InternalAlignment(g126,g128)
    c: InternalAlignment(g127,g128)
    c: InternalAlignment(g129,g128)
    c: InternalAlignment(g130,g128)
    c: Weight(g131) = 1
    c: Equal(g131,g132)
    c: Equal(g131,g133)
    c: InternalAlignment(g131,g134)
    c: InternalAlignment(g132,g134)
    c: InternalAlignment(g133,g134)
    c: InternalAlignment(g135,g134)
    c: InternalAlignment(g136,g134)
    c: Weight(g137) = 1
    c: Equal(g137,g138)
    c: Equal(g137,g139)
    c: InternalAlignment(g137,g140)
    c: InternalAlignment(g138,g140)
    c: InternalAlignment(g139,g140)
    c: InternalAlignment(g141,g140)
    c: InternalAlignment(g142,g140)
    c: Weight(g143) = 1
    c: Equal(g143,g144)
    c: Equal(g143,g145)
    c: InternalAlignment(g143,g146)
    c: InternalAlignment(g144,g146)
    c: InternalAlignment(g145,g146)
    c: InternalAlignment(g147,g146)
    c: InternalAlignment(g148,g146)
    c: Block(g146)
    c: Block(g140)
    c: Block(g134)
    c: Block(g128)
    c: Coincident(g149,g25)
    c: Coincident(g149,g146)
    c: Coincident(g150,g146)
    c: Coincident(g150,g140)
    c: Horizontal(g150)
    c: Coincident(g151,g140)
    c: Coincident(g151,g25)
    c: Vertical(g151)
    c: Coincident(g152,g19)
    c: Coincident(g152,g134)
    c: Vertical(g152)
    c: Coincident(g153,g134)
    c: Coincident(g153,g128)
    c: Horizontal(g153)
    c: Coincident(g154,g128)
    c: Coincident(g154,g19)
    c: Weight(g155) = 1
    c: Equal(g155,g156)
    c: Equal(g155,g157)
    c: InternalAlignment(g155,g158)
    c: InternalAlignment(g156,g158)
    c: InternalAlignment(g157,g158)
    c: InternalAlignment(g159,g158)
    c: InternalAlignment(g160,g158)
    c: Weight(g161) = 1
    c: Equal(g161,g162)
    c: Equal(g161,g163)
    c: InternalAlignment(g161,g164)
    c: InternalAlignment(g162,g164)
    c: InternalAlignment(g163,g164)
    c: InternalAlignment(g165,g164)
    c: InternalAlignment(g166,g164)
    c: Weight(g167) = 1
    c: Equal(g167,g168)
    c: Equal(g167,g169)
    c: InternalAlignment(g167,g170)
    c: InternalAlignment(g168,g170)
    c: InternalAlignment(g169,g170)
    c: InternalAlignment(g171,g170)
    c: InternalAlignment(g172,g170)
    c: Weight(g173) = 1
    c: Equal(g173,g174)
    c: Equal(g173,g175)
    c: InternalAlignment(g173,g176)
    c: InternalAlignment(g174,g176)
    c: InternalAlignment(g175,g176)
    c: InternalAlignment(g177,g176)
    c: InternalAlignment(g178,g176)
    c: Block(g176)
    c: Block(g170)
    c: Block(g164)
    c: Block(g158)
    c: Coincident(g179,g170)
    c: Coincident(g179,g7)
    c: Vertical(g179)
    c: Coincident(g180,g13)
    c: Coincident(g180,g164)
    c: Vertical(g180)
    c: Coincident(g181,g158)
    c: Coincident(g181,g13)
    c: Coincident(g182,g7)
    c: Weight(g183) = 1
    c: Equal(g183,g184)
    c: Equal(g183,g185)
    c: InternalAlignment(g183,g186)
    c: InternalAlignment(g184,g186)
    c: InternalAlignment(g185,g186)
    c: InternalAlignment(g187,g186)
    c: InternalAlignment(g188,g186)
    c: Weight(g189) = 1
    c: Equal(g189,g190)
    c: Equal(g189,g191)
    c: InternalAlignment(g189,g192)
    c: InternalAlignment(g190,g192)
    c: InternalAlignment(g191,g192)
    c: InternalAlignment(g193,g192)
    c: InternalAlignment(g194,g192)
    c: Block(g192)
    c: Block(g186)
    c: Coincident(g195,g192)
    c: Coincident(g195,g31)
    c: Coincident(g196,g31)
    c: Coincident(g196,g186)
    c: Coincident(g197,g186)
    c: Coincident(g197,g192)
    c: Vertical(g197)
    c: Weight(g198) = 1
    c: Equal(g198,g199)
    c: Equal(g198,g200)
    c: InternalAlignment(g198,g201)
    c: InternalAlignment(g199,g201)
    c: InternalAlignment(g200,g201)
    c: InternalAlignment(g202,g201)
    c: InternalAlignment(g203,g201)
    c: Weight(g204) = 1
    c: Equal(g204,g205)
    c: Equal(g204,g206)
    c: InternalAlignment(g204,g207)
    c: InternalAlignment(g205,g207)
    c: InternalAlignment(g206,g207)
    c: InternalAlignment(g208,g207)
    c: InternalAlignment(g209,g207)
    c: Block(g207)
    c: Block(g201)
    c: Coincident(g210,g201)
    c: Coincident(g210,g37)
    c: Coincident(g211,g37)
    c: Coincident(g211,g207)
    c: Coincident(g212,g207)
    c: Coincident(g212,g201)
    c: Vertical(g212)
    c: Horizontal(g213)
    c: Block(g213)
    c: Vertical(g214)
    c: Block(g214)
    c: Block(g215)
    c: Weight(g216) = 1
    c: Equal(g216,g217)
    c: Equal(g216,g218)
    c: InternalAlignment(g216,g219)
    c: InternalAlignment(g217,g219)
    c: InternalAlignment(g218,g219)
    c: InternalAlignment(g220,g219)
    c: InternalAlignment(g221,g219)
    c: Weight(g222) = 1
    c: Equal(g222,g223)
    c: Equal(g222,g224)
    c: InternalAlignment(g222,g225)
    c: InternalAlignment(g223,g225)
    c: InternalAlignment(g224,g225)
    c: InternalAlignment(g226,g225)
    c: InternalAlignment(g227,g225)
    c: Weight(g228) = 1
    c: Equal(g228,g229)
    c: Equal(g228,g230)
    c: InternalAlignment(g228,g231)
    c: InternalAlignment(g229,g231)
    c: InternalAlignment(g230,g231)
    c: InternalAlignment(g232,g231)
    c: InternalAlignment(g233,g231)
    c: Weight(g234) = 1
    c: Equal(g234,g235)
    c: Equal(g234,g236)
    c: InternalAlignment(g234,g237)
    c: InternalAlignment(g235,g237)
    c: InternalAlignment(g236,g237)
    c: InternalAlignment(g238,g237)
    c: InternalAlignment(g239,g237)
    c: Block(g219)
    c: Block(g225)
    c: Block(g231)
    c: Block(g237)
    c: Coincident(g240,g225)
    c: Coincident(g240,g219)
    c: Horizontal(g240)
    c: Block(g182)
    c: Weight(g241) = 1
    c: Equal(g241,g242)
    c: Equal(g241,g243)
    c: InternalAlignment(g241,g244)
    c: InternalAlignment(g242,g244)
    c: InternalAlignment(g243,g244)
    c: InternalAlignment(g245,g244)
    c: InternalAlignment(g246,g244)
    c: Weight(g247) = 1
    c: Equal(g247,g248)
    c: Equal(g247,g249)
    c: InternalAlignment(g247,g250)
    c: InternalAlignment(g248,g250)
    c: InternalAlignment(g249,g250)
    c: InternalAlignment(g251,g250)
    c: InternalAlignment(g252,g250)
    c: Block(g244)
    c: Block(g250)
    c: Coincident(g253,g244)
    c: Coincident(g253,g250)
    c: Weight(g254) = 1
    c: Equal(g254,g255)
    c: Equal(g254,g256)
    c: InternalAlignment(g254,g257)
    c: InternalAlignment(g255,g257)
    c: InternalAlignment(g256,g257)
    c: InternalAlignment(g258,g257)
    c: InternalAlignment(g259,g257)
    c: Weight(g260) = 1
    c: Equal(g260,g261)
    c: Equal(g260,g262)
    c: InternalAlignment(g260,g263)
    c: InternalAlignment(g261,g263)
    c: InternalAlignment(g262,g263)
    c: InternalAlignment(g264,g263)
    c: InternalAlignment(g265,g263)
    c: Weight(g266) = 1
    c: Equal(g266,g267)
    c: Equal(g266,g268)
    c: InternalAlignment(g266,g269)
    c: InternalAlignment(g267,g269)
    c: InternalAlignment(g268,g269)
    c: InternalAlignment(g270,g269)
    c: InternalAlignment(g271,g269)
    c: Block(g269)
    c: Block(g263)
    c: Block(g257)
    c: Coincident(g272,g263)
    c: Coincident(g272,g257)
    c: Coincident(g273,g257)
    c: Coincident(g273,g269)
    c: Vertical(g273)
    c: Coincident(g274,g269)
    c: Coincident(g274,g263)
    c: Horizontal(g274)
    c: Weight(g275) = 1
    c: Equal(g275,g276)
    c: InternalAlignment(g275,g277)
    c: InternalAlignment(g276,g277)
    c: InternalAlignment(g278,g277)
    c: InternalAlignment(g279,g277)
    c: Weight(g280) = 1
    c: InternalAlignment(g281,g283)
    c: InternalAlignment(g282,g283)
    c: InternalAlignment(g284,g283)
    c: InternalAlignment(g285,g283)
    c: Weight(g286) = 1
    c: Equal(g286,g287)
    c: Equal(g286,g288)
    c: InternalAlignment(g286,g289)
    c: InternalAlignment(g287,g289)
    c: InternalAlignment(g288,g289)
    c: InternalAlignment(g290,g289)
    c: InternalAlignment(g291,g289)
    c: Equal(g292,g293)
    c: Equal(g292,g294)
    c: InternalAlignment(g292,g295)
    c: InternalAlignment(g293,g295)
    c: InternalAlignment(g294,g295)
    c: InternalAlignment(g296,g295)
    c: InternalAlignment(g297,g295)
    c: Block(g283)
    c: Block(g289)
    c: Block(g295)
    c: Block(g277)
    c: Coincident(g298,g277)
    c: Coincident(g298,g283)
    c: Horizontal(g298)
    c: Coincident(g299,g283)
    c: Coincident(g299,g289)
    c: Vertical(g299)
    c: Coincident(g300,g289)
    c: Coincident(g300,g295)
    c: Horizontal(g300)
    c: Coincident(g301,g295)
    c: Coincident(g301,g277)
    c: Weight(g302) = 1
    c: Equal(g302,g303)
    c: Equal(g302,g304)
    c: InternalAlignment(g302,g305)
    c: InternalAlignment(g303,g305)
    c: InternalAlignment(g304,g305)
    c: InternalAlignment(g306,g305)
    c: InternalAlignment(g307,g305)
    c: Weight(g308) = 1
    c: Equal(g308,g309)
    c: Equal(g308,g310)
    c: InternalAlignment(g308,g311)
    c: InternalAlignment(g309,g311)
    c: InternalAlignment(g310,g311)
    c: InternalAlignment(g312,g311)
    c: Weight(g314) = 1
    c: Equal(g314,g315)
    c: Equal(g314,g316)
    c: InternalAlignment(g314,g317)
    c: InternalAlignment(g315,g317)
    c: InternalAlignment(g316,g317)
    c: InternalAlignment(g318,g317)
    c: InternalAlignment(g319,g317)
    c: Block(g317)
    c: Block(g311)
    c: Block(g305)
    c: Coincident(g320,g317)
    c: Coincident(g320,g311)
    c: Horizontal(g320)
    c: Coincident(g321,g311)
    c: Coincident(g321,g305)
    c: Vertical(g321)
    c: Coincident(g322,g305)
    c: Coincident(g322,g317)
    c: InternalAlignment(g323,g324)
    c: InternalAlignment(g325,g324)
    c: InternalAlignment(g326,g324)
    c: Block(g324)
    c: Equal(g327,g328)
    c: Equal(g327,g329)
    c: InternalAlignment(g327,g330)
    c: InternalAlignment(g328,g330)
    c: InternalAlignment(g329,g330)
    c: InternalAlignment(g331,g330)
    c: InternalAlignment(g332,g330)
    c: Block(g330)
    c: Coincident(g333,g324)
    c: Horizontal(g333)
    c: Block(g333)
    c: Coincident(g334,g324)
    c: Coincident(g334,g250)
    c: Vertical(g334)
    c: Coincident(g335,g330)
    c: Coincident(g335,g244)
    c: Vertical(g335)
    c: Block(g336)
    c: Block(g2)
    c: Distance(g334) = 119.89
    c: Coincident(g337,g336)
    c: Coincident(g337,g2)
    c: Coincident(g338,g2)
    c: Coincident(g338,g336)
    c: Block(g3)
    c: Block(g339)
    c: Coincident(g340,g339)
    c: Coincident(g340,g3)
    c: Coincident(g341,g339)
    c: Coincident(g341,g3)
    c: Block(g341)
    c: Block(g340)
    c: Weight(g342) = 1
    c: Equal(g342,g343)
    c: Equal(g342,g344)
    c: InternalAlignment(g342,g345)
    c: InternalAlignment(g343,g345)
    c: InternalAlignment(g344,g345)
    c: InternalAlignment(g346,g345)
    c: InternalAlignment(g347,g345)
    c: Weight(g348) = 1
    c: Equal(g348,g349)
    c: Equal(g348,g350)
    c: InternalAlignment(g348,g351)
    c: InternalAlignment(g349,g351)
    c: InternalAlignment(g350,g351)
    c: InternalAlignment(g352,g351)
    c: InternalAlignment(g353,g351)
    c: Weight(g354) = 1
    c: Equal(g354,g355)
    c: Equal(g354,g356)
    c: InternalAlignment(g354,g357)
    c: InternalAlignment(g355,g357)
    c: InternalAlignment(g356,g357)
    c: InternalAlignment(g358,g357)
    c: InternalAlignment(g359,g357)
    c: Weight(g360) = 1
    c: Equal(g360,g361)
    c: Equal(g360,g362)
    c: InternalAlignment(g360,g363)
    c: InternalAlignment(g361,g363)
    c: InternalAlignment(g362,g363)
    c: InternalAlignment(g364,g363)
    c: InternalAlignment(g365,g363)
    c: Block(g363)
    c: Block(g357)
    c: Block(g351)
    c: Block(g345)
    c: Coincident(g366,g363)
    c: Coincident(g366,g345)
    c: Vertical(g366)
    c: Coincident(g367,g345)
    c: Coincident(g367,g351)
    c: Coincident(g368,g351)
    c: Coincident(g368,g357)
    c: Vertical(g368)
    c: Coincident(g369,g357)
    c: Coincident(g369,g363)
    c: Horizontal(g369)
    c: Vertical(g370)
    c: Coincident(g371,g0)
    c: Coincident(g371,g1)
    c: Horizontal(g371)
    c: Block(g371)
    c: Distance(g371) = 450
    c: Block(g370)
    c: Distance(g0) = 240
    c: Horizontal(g372)
    c: Distance(g372) = 12
    c: Vertical(g373)
    c: Distance(g373) = 12
    c: Coincident(g374,g372)
    c: Vertical(g374)
    c: Horizontal(g375)
    c: Vertical(g376)
    c: Distance(g376) = 6
    c: Coincident(g376,g372)
    c: Coincident(g375,g372)
    c: Block(g374)
    c: Coincident(g377,g374)
    c: Horizontal(g377)
    c: Distance(g377) = 6
    c: Vertical(g378)
    c: Distance(g378) = 3
    c: Vertical(g379)
    c: Distance(g379) = 3
    c: Coincident(g373,g378)
    c: Coincident(g385,g379)
    c: Weight(g380) = 1
    c: Equal(g380,g381)
    c: Coincident(g381,g375)
    c: Equal(g380,g382)
    c: Coincident(g382,g376)
    c: Equal(g380,g383)
    c: Coincident(g383,g377)
    c: Equal(g380,g384)
    c: Coincident(g385,g378)
    c: InternalAlignment(g380-g384 -> g385) x5
    c: InternalAlignment(g386,g385)
    c: InternalAlignment(g387,g385)
    c: InternalAlignment(g388,g385)
    c: Coincident(g389,g164)
    c: Coincident(g389,g158)
    c: Horizontal(g389)
    c: Block(g385)
    c: Vertical(g390)
    c: Distance(g390) = 12
    c: Horizontal(g391)
    c: Distance(g391) = 12
    c: Coincident(g392,g391)
    c: Vertical(g392)
    c: Distance(g392) = 12
    c: Horizontal(g393)
    c: Distance(g393) = 6
    c: Coincident(g393,g391)
    c: Vertical(g394)
    c: Distance(g394) = 6
    c: Coincident(g394,g391)
    c: Vertical(g395)
    c: Distance(g395) = 3
    c: Vertical(g396)
    c: Distance(g396) = 6
    c: Coincident(g396,g395)
    c: Coincident(g402,g395)
    c: Weight(g397) = 1
    c: Equal(g397,g398)
    c: Coincident(g398,g393)
    c: Equal(g397,g399)
    c: Coincident(g399,g394)
    c: Equal(g397,g400)
    c: Equal(g397,g401)
    c: Coincident(g402,g396)
    c: InternalAlignment(g397-g401 -> g402) x5
    c: InternalAlignment(g403,g402)
    c: InternalAlignment(g404,g402)
    c: InternalAlignment(g405,g402)
    c: Coincident(g406,g390)
    c: Coincident(g406,g170)
    c: Horizontal(g406)
    c: Block(g402)
    c: Coincident(g407,g176)
    c: Coincident(g407,g390)
    c: Horizontal(g407)
    c: Block(g406)
    c: Coincident(g409,g390)
    c: PointOnObject(g409,g153)
    c: Vertical(g409)
    c: Block(g410)
    c: Coincident(g411,g410)
    c: Vertical(g411)
    c: PointOnObject(g411,g40)
    c: Block(g411)
    c: Coincident(g412,g410)
    c: Vertical(g412)
    c: Block(g412)
    c: Vertical(g413)
    c: Distance(g413) = 3
    c: Equal(g380,g416) = 1
    c: Equal(g416,g417)
    c: InternalAlignment(g416,g418)
    c: InternalAlignment(g417,g418)
    c: InternalAlignment(g414,g418)
    c: InternalAlignment(g415,g418)
    c: InternalAlignment(g419,g418)
    c: Block(g418)
    c: Coincident(g419,g413)
    c: Coincident(g420,g418)
    c: PointOnObject(g420,g150)
    c: Vertical(g420)
    c: PointOnObject(g421,g211)
    c: Block(g421)
    c: Distance(g422) = 3
    c: Block(g422)
    c: Distance(g423) = 3
    c: Parallel(g423,g422)
    c: Coincident(g423,g422)
    c: Coincident(g424,g422)
    c: Perpendicular(g424,g422)
    c: Distance(g424) = 3
    c: Coincident(g425,g423)
    c: Perpendicular(g425,g423)
    c: Distance(g425) = 3
    c: Coincident(g426,g422)
    c: Perpendicular(g426,g423)
    c: Distance(g426) = 5
FEATURE [Part::Extrusion] Extrude005
  Base = -> Sketch003
  Dir = (0,0,1)
  DirMode = 2
  FaceMakerClass = Part::FaceMakerBullseye
  LengthFwd = 24
  LengthRev = 0
  Solid = true
  Symmetric = false
